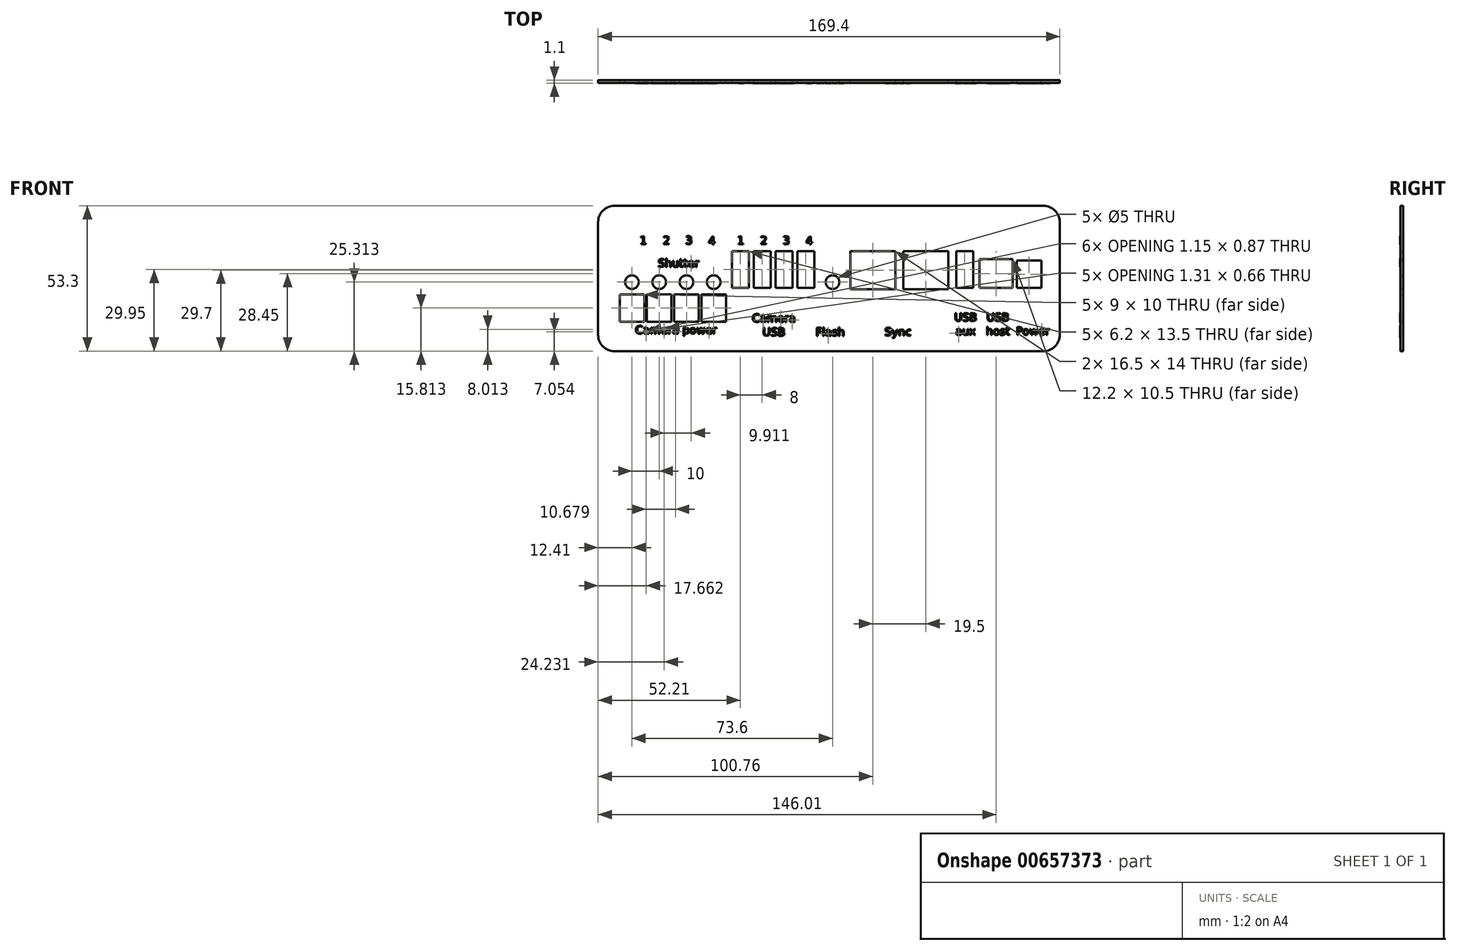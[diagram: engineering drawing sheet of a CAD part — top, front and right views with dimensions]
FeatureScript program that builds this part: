
annotation { "Feature Type Name" : "Feature", "Feature Type Description" : "" }
export const myFeature = defineFeature(function(context is Context, id is Id, definition is map)
    precondition{}
    {
        {
            var Q0;
            Q0=qCreatedBy(makeId("Front.planeOp"),FACE);
            var sketch = newSketch(context, id + "F0", { "sketchPlane" : qUnion([Q0])});
            skLineSegment(sketch, "E0", {"start": v(-108.51, -23.45) * mm, "end": v(48.89, -23.45) * mm});
            skLineSegment(sketch, "E1", {"start": v(48.89, 29.85) * mm, "end": v(-108.51, 29.85) * mm});
            skArc(sketch, "E2", {"start": v(-114.51, -17.45) * mm, "mid": v(-112.76, -21.7) * mm, "end": v(-108.51, -23.45) * mm});
            skLineSegment(sketch, "E3", {"start": v(54.89, -17.45) * mm, "end": v(54.89, 23.85) * mm});
            skArc(sketch, "E4", {"start": v(48.89, -23.45) * mm, "mid": v(53.13, -21.7) * mm, "end": v(54.89, -17.45) * mm});
            skArc(sketch, "E5", {"start": v(54.89, 23.85) * mm, "mid": v(53.13, 28.1) * mm, "end": v(48.89, 29.85) * mm});
            skLineSegment(sketch, "E6", {"start": v(-114.51, 23.85) * mm, "end": v(-114.51, -17.45) * mm});
            skArc(sketch, "E7", {"start": v(-108.51, 29.85) * mm, "mid": v(-112.76, 28.1) * mm, "end": v(-114.51, 23.85) * mm});
            skLineSegment(sketch, "E8.bottom", {"start": v(-59.2, -0.25) * mm, "end": v(-65.4, -0.25) * mm});
            skLineSegment(sketch, "E8.top", {"start": v(-59.2, 13.25) * mm, "end": v(-65.4, 13.25) * mm});
            skLineSegment(sketch, "E8.left", {"start": v(-59.2, -0.25) * mm, "end": v(-59.2, 13.25) * mm});
            skLineSegment(sketch, "E8.right", {"start": v(-65.4, -0.25) * mm, "end": v(-65.4, 13.25) * mm});
            skPoint(sketch, "E8.middle", {"position": v(-62.3, 6.5) * mm});
            skCircle(sketch, "E9", {"center": v(-72.1, 1.86) * mm, "radius": 2.5 * mm});
            skLineSegment(sketch, "E10.bottom", {"start": v(-67.6, -12.64) * mm, "end": v(-76.6, -12.64) * mm});
            skLineSegment(sketch, "E10.top", {"start": v(-67.6, -2.64) * mm, "end": v(-76.6, -2.64) * mm});
            skLineSegment(sketch, "E10.left", {"start": v(-67.6, -12.64) * mm, "end": v(-67.6, -2.64) * mm});
            skLineSegment(sketch, "E10.right", {"start": v(-76.6, -12.64) * mm, "end": v(-76.6, -2.64) * mm});
            skPoint(sketch, "E10.middle", {"position": v(-72.1, -7.64) * mm});
            skCircle(sketch, "E11.1.0.0", {"center": v(-82.1, 1.86) * mm, "radius": 2.5 * mm});
            skLineSegment(sketch, "E11.1.0.1", {"start": v(-77.6, -2.64) * mm, "end": v(-86.6, -2.64) * mm});
            skLineSegment(sketch, "E11.1.0.2", {"start": v(-77.6, -12.64) * mm, "end": v(-77.6, -2.64) * mm});
            skLineSegment(sketch, "E11.1.0.3", {"start": v(-77.6, -12.64) * mm, "end": v(-86.6, -12.64) * mm});
            skLineSegment(sketch, "E11.1.0.4", {"start": v(-86.6, -12.64) * mm, "end": v(-86.6, -2.64) * mm});
            skCircle(sketch, "E11.2.0.0", {"center": v(-92.1, 1.86) * mm, "radius": 2.5 * mm});
            skLineSegment(sketch, "E11.2.0.1", {"start": v(-87.6, -2.64) * mm, "end": v(-96.6, -2.64) * mm});
            skLineSegment(sketch, "E11.2.0.2", {"start": v(-87.6, -12.64) * mm, "end": v(-87.6, -2.64) * mm});
            skLineSegment(sketch, "E11.2.0.3", {"start": v(-87.6, -12.64) * mm, "end": v(-96.6, -12.64) * mm});
            skLineSegment(sketch, "E11.2.0.4", {"start": v(-96.6, -12.64) * mm, "end": v(-96.6, -2.64) * mm});
            skCircle(sketch, "E11.3.0.0", {"center": v(-102.1, 1.86) * mm, "radius": 2.5 * mm});
            skLineSegment(sketch, "E11.3.0.1", {"start": v(-97.6, -2.64) * mm, "end": v(-106.6, -2.64) * mm});
            skLineSegment(sketch, "E11.3.0.2", {"start": v(-97.6, -12.64) * mm, "end": v(-97.6, -2.64) * mm});
            skLineSegment(sketch, "E11.3.0.3", {"start": v(-97.6, -12.64) * mm, "end": v(-106.6, -12.64) * mm});
            skLineSegment(sketch, "E11.3.0.4", {"start": v(-106.6, -12.64) * mm, "end": v(-106.6, -2.64) * mm});
            skLineSegment(sketch, "E11.direction1", {"start": v(-72.1, 1.86) * mm, "end": v(-82.1, 1.86) * mm, "construction": true});
            skLineSegment(sketch, "E12.1.0.0", {"start": v(-51.2, -0.25) * mm, "end": v(-51.2, 13.25) * mm});
            skLineSegment(sketch, "E12.1.0.1", {"start": v(-51.2, 13.25) * mm, "end": v(-57.4, 13.25) * mm});
            skLineSegment(sketch, "E12.1.0.2", {"start": v(-57.4, -0.25) * mm, "end": v(-57.4, 13.25) * mm});
            skLineSegment(sketch, "E12.1.0.3", {"start": v(-51.2, -0.25) * mm, "end": v(-57.4, -0.25) * mm});
            skLineSegment(sketch, "E12.2.0.0", {"start": v(-43.2, -0.25) * mm, "end": v(-43.2, 13.25) * mm});
            skLineSegment(sketch, "E12.2.0.1", {"start": v(-43.2, 13.25) * mm, "end": v(-49.4, 13.25) * mm});
            skLineSegment(sketch, "E12.2.0.2", {"start": v(-49.4, -0.25) * mm, "end": v(-49.4, 13.25) * mm});
            skLineSegment(sketch, "E12.2.0.3", {"start": v(-43.2, -0.25) * mm, "end": v(-49.4, -0.25) * mm});
            skLineSegment(sketch, "E12.3.0.0", {"start": v(-35.2, -0.25) * mm, "end": v(-35.2, 13.25) * mm});
            skLineSegment(sketch, "E12.3.0.1", {"start": v(-35.2, 13.25) * mm, "end": v(-41.4, 13.25) * mm});
            skLineSegment(sketch, "E12.3.0.2", {"start": v(-41.4, -0.25) * mm, "end": v(-41.4, 13.25) * mm});
            skLineSegment(sketch, "E12.3.0.3", {"start": v(-35.2, -0.25) * mm, "end": v(-41.4, -0.25) * mm});
            skLineSegment(sketch, "E12.direction1", {"start": v(-59.2, -0.25) * mm, "end": v(-51.2, -0.25) * mm, "construction": true});
            skCircle(sketch, "E13", {"center": v(-28.5, 1.86) * mm, "radius": 2.5 * mm});
            skLineSegment(sketch, "E14.bottom", {"start": v(-5.5, 13.25) * mm, "end": v(-22, 13.25) * mm});
            skLineSegment(sketch, "E14.top", {"start": v(-5.5, -0.75) * mm, "end": v(-22, -0.75) * mm});
            skLineSegment(sketch, "E14.left", {"start": v(-5.5, 13.25) * mm, "end": v(-5.5, -0.75) * mm});
            skLineSegment(sketch, "E14.right", {"start": v(-22, 13.25) * mm, "end": v(-22, -0.75) * mm});
            skPoint(sketch, "E14.middle", {"position": v(-13.75, 6.25) * mm});
            skPoint(sketch, "E15.1.0.0", {"position": v(5.75, 6.25) * mm});
            skLineSegment(sketch, "E15.1.0.1", {"start": v(14, 13.25) * mm, "end": v(-2.5, 13.25) * mm});
            skLineSegment(sketch, "E15.1.0.2", {"start": v(14, 13.25) * mm, "end": v(14, -0.75) * mm});
            skLineSegment(sketch, "E15.1.0.3", {"start": v(14, -0.75) * mm, "end": v(-2.5, -0.75) * mm});
            skLineSegment(sketch, "E15.1.0.4", {"start": v(-2.5, 13.25) * mm, "end": v(-2.5, -0.75) * mm});
            skLineSegment(sketch, "E15.direction1", {"start": v(-13.75, 6.25) * mm, "end": v(5.75, 6.25) * mm, "construction": true});
            skLineSegment(sketch, "E16.bottom", {"start": v(23.1, -0.25) * mm, "end": v(16.9, -0.25) * mm});
            skLineSegment(sketch, "E16.top", {"start": v(23.1, 13.25) * mm, "end": v(16.9, 13.25) * mm});
            skLineSegment(sketch, "E16.left", {"start": v(23.1, -0.25) * mm, "end": v(23.1, 13.25) * mm});
            skLineSegment(sketch, "E16.right", {"start": v(16.9, -0.25) * mm, "end": v(16.9, 13.25) * mm});
            skPoint(sketch, "E16.middle", {"position": v(20, 6.5) * mm});
            skLineSegment(sketch, "E17.bottom", {"start": v(37.6, 10.25) * mm, "end": v(25.4, 10.25) * mm});
            skLineSegment(sketch, "E17.top", {"start": v(37.6, -0.25) * mm, "end": v(25.4, -0.25) * mm});
            skLineSegment(sketch, "E17.left", {"start": v(37.6, 10.25) * mm, "end": v(37.6, -0.25) * mm});
            skLineSegment(sketch, "E17.right", {"start": v(25.4, 10.25) * mm, "end": v(25.4, -0.25) * mm});
            skPoint(sketch, "E17.middle", {"position": v(31.5, 5) * mm});
            skLineSegment(sketch, "E18.bottom", {"start": v(48.1, -0.25) * mm, "end": v(39.1, -0.25) * mm});
            skLineSegment(sketch, "E18.top", {"start": v(48.1, 9.75) * mm, "end": v(39.1, 9.75) * mm});
            skLineSegment(sketch, "E18.left", {"start": v(48.1, -0.25) * mm, "end": v(48.1, 9.75) * mm});
            skLineSegment(sketch, "E18.right", {"start": v(39.1, -0.25) * mm, "end": v(39.1, 9.75) * mm});
            skPoint(sketch, "E18.middle", {"position": v(43.6, 4.75) * mm});
            skSolve(sketch);
        }
        {
            var Q0;
            Q0=makeQuery(id+"F0.imprint","IMPRINT",FACE,{"disambiguationData":[TD([[makeQuery(id+"F0.imprint","IMPRINT",EDGE,{"derivedFrom":sQuery(id+"F0.wireOp",EDGE,"E0")}),1.0]])]});
            extrude(context, id + "F1", {"entities" : qUnion([Q0]), "depth" : 1 * mm, "offsetDistance" : 25 * mm});
        }
        {
            var Q0;
            Q0=makeQuery(id+"F1.opExtrude","CAP_FACE",FACE,{"disambiguationData":[OSD([sQuery(id+"F0.wireOp",EDGE,"E0"),sQuery(id+"F0.wireOp",EDGE,"E1"),sQuery(id+"F0.wireOp",EDGE,"E2"),sQuery(id+"F0.wireOp",EDGE,"E3"),sQuery(id+"F0.wireOp",EDGE,"E4"),sQuery(id+"F0.wireOp",EDGE,"E5"),sQuery(id+"F0.wireOp",EDGE,"E6"),sQuery(id+"F0.wireOp",EDGE,"E7"),sQuery(id+"F0.wireOp",EDGE,"E8.bottom"),sQuery(id+"F0.wireOp",EDGE,"E8.top"),sQuery(id+"F0.wireOp",EDGE,"E8.left"),sQuery(id+"F0.wireOp",EDGE,"E8.right"),sQuery(id+"F0.wireOp",EDGE,"E9"),sQuery(id+"F0.wireOp",EDGE,"E10.bottom"),sQuery(id+"F0.wireOp",EDGE,"E10.top"),sQuery(id+"F0.wireOp",EDGE,"E10.left"),sQuery(id+"F0.wireOp",EDGE,"E10.right"),sQuery(id+"F0.wireOp",EDGE,"E11.1.0.0"),sQuery(id+"F0.wireOp",EDGE,"E11.1.0.1"),sQuery(id+"F0.wireOp",EDGE,"E11.1.0.2"),sQuery(id+"F0.wireOp",EDGE,"E11.1.0.3"),sQuery(id+"F0.wireOp",EDGE,"E11.1.0.4"),sQuery(id+"F0.wireOp",EDGE,"E11.2.0.0"),sQuery(id+"F0.wireOp",EDGE,"E11.2.0.1"),sQuery(id+"F0.wireOp",EDGE,"E11.2.0.2"),sQuery(id+"F0.wireOp",EDGE,"E11.2.0.3"),sQuery(id+"F0.wireOp",EDGE,"E11.2.0.4"),sQuery(id+"F0.wireOp",EDGE,"E11.3.0.0"),sQuery(id+"F0.wireOp",EDGE,"E11.3.0.1"),sQuery(id+"F0.wireOp",EDGE,"E11.3.0.2"),sQuery(id+"F0.wireOp",EDGE,"E11.3.0.3"),sQuery(id+"F0.wireOp",EDGE,"E11.3.0.4"),sQuery(id+"F0.wireOp",EDGE,"E12.1.0.0"),sQuery(id+"F0.wireOp",EDGE,"E12.1.0.1"),sQuery(id+"F0.wireOp",EDGE,"E12.1.0.2"),sQuery(id+"F0.wireOp",EDGE,"E12.1.0.3"),sQuery(id+"F0.wireOp",EDGE,"E12.2.0.0"),sQuery(id+"F0.wireOp",EDGE,"E12.2.0.1"),sQuery(id+"F0.wireOp",EDGE,"E12.2.0.2"),sQuery(id+"F0.wireOp",EDGE,"E12.2.0.3"),sQuery(id+"F0.wireOp",EDGE,"E12.3.0.0"),sQuery(id+"F0.wireOp",EDGE,"E12.3.0.1"),sQuery(id+"F0.wireOp",EDGE,"E12.3.0.2"),sQuery(id+"F0.wireOp",EDGE,"E12.3.0.3"),sQuery(id+"F0.wireOp",EDGE,"E13"),sQuery(id+"F0.wireOp",EDGE,"E14.bottom"),sQuery(id+"F0.wireOp",EDGE,"E14.top"),sQuery(id+"F0.wireOp",EDGE,"E14.left"),sQuery(id+"F0.wireOp",EDGE,"E14.right"),sQuery(id+"F0.wireOp",EDGE,"E15.1.0.1"),sQuery(id+"F0.wireOp",EDGE,"E15.1.0.2"),sQuery(id+"F0.wireOp",EDGE,"E15.1.0.3"),sQuery(id+"F0.wireOp",EDGE,"E15.1.0.4"),sQuery(id+"F0.wireOp",EDGE,"E16.bottom"),sQuery(id+"F0.wireOp",EDGE,"E16.top"),sQuery(id+"F0.wireOp",EDGE,"E16.left"),sQuery(id+"F0.wireOp",EDGE,"E16.right"),sQuery(id+"F0.wireOp",EDGE,"E17.bottom"),sQuery(id+"F0.wireOp",EDGE,"E17.top"),sQuery(id+"F0.wireOp",EDGE,"E17.left"),sQuery(id+"F0.wireOp",EDGE,"E17.right"),sQuery(id+"F0.wireOp",EDGE,"E18.bottom"),sQuery(id+"F0.wireOp",EDGE,"E18.top"),sQuery(id+"F0.wireOp",EDGE,"E18.left"),sQuery(id+"F0.wireOp",EDGE,"E18.right")])],"isStart":false});
            var sketch = newSketch(context, id + "F2", { "sketchPlane" : qUnion([Q0])});
            skLineSegment(sketch, "E19", {"start": v(-62.99, 16.07) * mm, "end": v(-62.33, 16.07) * mm});
            skLineSegment(sketch, "E20", {"start": v(-62.33, 16.07) * mm, "end": v(-62.33, 18.34) * mm});
            skLineSegment(sketch, "E21", {"start": v(-62.33, 18.34) * mm, "end": v(-63.05, 18.2) * mm});
            skLineSegment(sketch, "E22", {"start": v(-63.05, 18.2) * mm, "end": v(-63.05, 18.57) * mm});
            skLineSegment(sketch, "E23", {"start": v(-63.05, 18.57) * mm, "end": v(-62.33, 18.71) * mm});
            skLineSegment(sketch, "E24", {"start": v(-62.33, 18.71) * mm, "end": v(-61.93, 18.71) * mm});
            skLineSegment(sketch, "E25", {"start": v(-61.93, 18.71) * mm, "end": v(-61.93, 16.07) * mm});
            skLineSegment(sketch, "E26", {"start": v(-61.93, 16.07) * mm, "end": v(-61.27, 16.07) * mm});
            skLineSegment(sketch, "E27", {"start": v(-61.27, 16.07) * mm, "end": v(-61.27, 15.73) * mm});
            skLineSegment(sketch, "E28", {"start": v(-61.27, 15.73) * mm, "end": v(-62.99, 15.73) * mm});
            skLineSegment(sketch, "E29", {"start": v(-62.99, 15.73) * mm, "end": v(-62.99, 16.07) * mm});
            skLineSegment(sketch, "E30", {"start": v(-54.25, 16.05) * mm, "end": v(-52.85, 16.05) * mm});
            skLineSegment(sketch, "E31", {"start": v(-52.85, 16.05) * mm, "end": v(-52.85, 15.7) * mm});
            skLineSegment(sketch, "E32", {"start": v(-52.85, 15.7) * mm, "end": v(-54.74, 15.7) * mm});
            skLineSegment(sketch, "E33", {"start": v(-54.74, 15.7) * mm, "end": v(-54.74, 16.05) * mm});
            skLineSegment(sketch, "E34", {"start": v(-54.74, 16.05) * mm, "end": v(-54.11, 16.68) * mm});
            skLineSegment(sketch, "E35", {"start": v(-54.11, 16.68) * mm, "end": v(-53.61, 17.2) * mm});
            skLineSegment(sketch, "E36", {"start": v(-53.61, 17.2) * mm, "end": v(-53.34, 17.56) * mm});
            skLineSegment(sketch, "E37", {"start": v(-53.34, 17.56) * mm, "end": v(-53.27, 17.86) * mm});
            skLineSegment(sketch, "E38", {"start": v(-53.27, 17.86) * mm, "end": v(-53.43, 18.25) * mm});
            skLineSegment(sketch, "E39", {"start": v(-53.43, 18.25) * mm, "end": v(-53.87, 18.4) * mm});
            skLineSegment(sketch, "E40", {"start": v(-53.87, 18.4) * mm, "end": v(-54.27, 18.33) * mm});
            skLineSegment(sketch, "E41", {"start": v(-54.27, 18.33) * mm, "end": v(-54.72, 18.13) * mm});
            skLineSegment(sketch, "E42", {"start": v(-54.72, 18.13) * mm, "end": v(-54.72, 18.54) * mm});
            skLineSegment(sketch, "E43", {"start": v(-54.72, 18.54) * mm, "end": v(-54.26, 18.69) * mm});
            skLineSegment(sketch, "E44", {"start": v(-54.26, 18.69) * mm, "end": v(-53.87, 18.74) * mm});
            skLineSegment(sketch, "E45", {"start": v(-53.87, 18.74) * mm, "end": v(-53.14, 18.5) * mm});
            skLineSegment(sketch, "E46", {"start": v(-53.14, 18.5) * mm, "end": v(-52.86, 17.89) * mm});
            skLineSegment(sketch, "E47", {"start": v(-52.86, 17.89) * mm, "end": v(-52.93, 17.54) * mm});
            skLineSegment(sketch, "E48", {"start": v(-52.93, 17.54) * mm, "end": v(-53.18, 17.15) * mm});
            skLineSegment(sketch, "E49", {"start": v(-53.18, 17.15) * mm, "end": v(-53.5, 16.82) * mm});
            skLineSegment(sketch, "E50", {"start": v(-53.5, 16.82) * mm, "end": v(-54.25, 16.05) * mm});
            skLineSegment(sketch, "E51", {"start": v(-45.05, 17.34) * mm, "end": v(-44.6, 17.08) * mm});
            skLineSegment(sketch, "E52", {"start": v(-44.6, 17.08) * mm, "end": v(-44.44, 16.6) * mm});
            skLineSegment(sketch, "E53", {"start": v(-44.44, 16.6) * mm, "end": v(-44.74, 15.92) * mm});
            skLineSegment(sketch, "E54", {"start": v(-44.74, 15.92) * mm, "end": v(-45.6, 15.68) * mm});
            skLineSegment(sketch, "E55", {"start": v(-45.6, 15.68) * mm, "end": v(-46, 15.72) * mm});
            skLineSegment(sketch, "E56", {"start": v(-46, 15.72) * mm, "end": v(-46.4, 15.83) * mm});
            skLineSegment(sketch, "E57", {"start": v(-46.4, 15.83) * mm, "end": v(-46.4, 16.21) * mm});
            skLineSegment(sketch, "E58", {"start": v(-46.4, 16.21) * mm, "end": v(-46.03, 16.07) * mm});
            skLineSegment(sketch, "E59", {"start": v(-46.03, 16.07) * mm, "end": v(-45.62, 16.02) * mm});
            skLineSegment(sketch, "E60", {"start": v(-45.62, 16.02) * mm, "end": v(-45.04, 16.17) * mm});
            skLineSegment(sketch, "E61", {"start": v(-45.04, 16.17) * mm, "end": v(-44.84, 16.6) * mm});
            skLineSegment(sketch, "E62", {"start": v(-44.84, 16.6) * mm, "end": v(-45.03, 17.01) * mm});
            skLineSegment(sketch, "E63", {"start": v(-45.03, 17.01) * mm, "end": v(-45.54, 17.16) * mm});
            skLineSegment(sketch, "E64", {"start": v(-45.54, 17.16) * mm, "end": v(-45.89, 17.16) * mm});
            skLineSegment(sketch, "E65", {"start": v(-45.89, 17.16) * mm, "end": v(-45.89, 17.5) * mm});
            skLineSegment(sketch, "E66", {"start": v(-45.89, 17.5) * mm, "end": v(-45.52, 17.5) * mm});
            skLineSegment(sketch, "E67", {"start": v(-45.52, 17.5) * mm, "end": v(-45.07, 17.61) * mm});
            skLineSegment(sketch, "E68", {"start": v(-45.07, 17.61) * mm, "end": v(-44.91, 17.95) * mm});
            skLineSegment(sketch, "E69", {"start": v(-44.91, 17.95) * mm, "end": v(-45.07, 18.3) * mm});
            skLineSegment(sketch, "E70", {"start": v(-45.07, 18.3) * mm, "end": v(-45.54, 18.43) * mm});
            skLineSegment(sketch, "E71", {"start": v(-45.54, 18.43) * mm, "end": v(-45.9, 18.4) * mm});
            skLineSegment(sketch, "E72", {"start": v(-45.9, 18.4) * mm, "end": v(-46.31, 18.28) * mm});
            skLineSegment(sketch, "E73", {"start": v(-46.31, 18.28) * mm, "end": v(-46.31, 18.64) * mm});
            skLineSegment(sketch, "E74", {"start": v(-46.31, 18.64) * mm, "end": v(-45.88, 18.73) * mm});
            skLineSegment(sketch, "E75", {"start": v(-45.88, 18.73) * mm, "end": v(-45.5, 18.77) * mm});
            skLineSegment(sketch, "E76", {"start": v(-45.5, 18.77) * mm, "end": v(-44.78, 18.56) * mm});
            skLineSegment(sketch, "E77", {"start": v(-44.78, 18.56) * mm, "end": v(-44.51, 18) * mm});
            skLineSegment(sketch, "E78", {"start": v(-44.51, 18) * mm, "end": v(-44.65, 17.58) * mm});
            skLineSegment(sketch, "E79", {"start": v(-44.65, 17.58) * mm, "end": v(-45.05, 17.34) * mm});
            skLineSegment(sketch, "E80", {"start": v(-36.8, 18.22) * mm, "end": v(-37.8, 16.63) * mm});
            skLineSegment(sketch, "E81", {"start": v(-37.8, 16.63) * mm, "end": v(-36.8, 16.63) * mm});
            skLineSegment(sketch, "E82", {"start": v(-36.8, 16.63) * mm, "end": v(-36.8, 18.22) * mm});
            skLineSegment(sketch, "E83", {"start": v(-36.9, 18.57) * mm, "end": v(-36.4, 18.57) * mm});
            skLineSegment(sketch, "E84", {"start": v(-36.4, 18.57) * mm, "end": v(-36.4, 16.63) * mm});
            skLineSegment(sketch, "E85", {"start": v(-36.4, 16.63) * mm, "end": v(-35.97, 16.63) * mm});
            skLineSegment(sketch, "E86", {"start": v(-35.97, 16.63) * mm, "end": v(-35.97, 16.3) * mm});
            skLineSegment(sketch, "E87", {"start": v(-35.97, 16.3) * mm, "end": v(-36.4, 16.3) * mm});
            skLineSegment(sketch, "E88", {"start": v(-36.4, 16.3) * mm, "end": v(-36.4, 15.6) * mm});
            skLineSegment(sketch, "E89", {"start": v(-36.4, 15.6) * mm, "end": v(-36.8, 15.6) * mm});
            skLineSegment(sketch, "E90", {"start": v(-36.8, 15.6) * mm, "end": v(-36.8, 16.3) * mm});
            skLineSegment(sketch, "E91", {"start": v(-36.8, 16.3) * mm, "end": v(-38.14, 16.3) * mm});
            skLineSegment(sketch, "E92", {"start": v(-38.14, 16.3) * mm, "end": v(-38.14, 16.69) * mm});
            skLineSegment(sketch, "E93", {"start": v(-38.14, 16.69) * mm, "end": v(-36.9, 18.57) * mm});
            skLineSegment(sketch, "E94", {"start": v(-98.26, -14.33) * mm, "end": v(-98.26, -14.76) * mm});
            skLineSegment(sketch, "E95", {"start": v(-98.26, -14.76) * mm, "end": v(-98.7, -14.48) * mm});
            skLineSegment(sketch, "E96", {"start": v(-98.7, -14.48) * mm, "end": v(-99.19, -14.38) * mm});
            skLineSegment(sketch, "E97", {"start": v(-99.19, -14.38) * mm, "end": v(-99.97, -14.7) * mm});
            skLineSegment(sketch, "E98", {"start": v(-99.97, -14.7) * mm, "end": v(-100.24, -15.6) * mm});
            skLineSegment(sketch, "E99", {"start": v(-100.24, -15.6) * mm, "end": v(-99.97, -16.5) * mm});
            skLineSegment(sketch, "E100", {"start": v(-99.97, -16.5) * mm, "end": v(-99.19, -16.8) * mm});
            skLineSegment(sketch, "E101", {"start": v(-99.19, -16.8) * mm, "end": v(-98.7, -16.72) * mm});
            skLineSegment(sketch, "E102", {"start": v(-98.7, -16.72) * mm, "end": v(-98.26, -16.43) * mm});
            skLineSegment(sketch, "E103", {"start": v(-98.26, -16.43) * mm, "end": v(-98.26, -16.85) * mm});
            skLineSegment(sketch, "E104", {"start": v(-98.26, -16.85) * mm, "end": v(-98.71, -17.07) * mm});
            skLineSegment(sketch, "E105", {"start": v(-98.71, -17.07) * mm, "end": v(-99.2, -17.14) * mm});
            skLineSegment(sketch, "E106", {"start": v(-99.2, -17.14) * mm, "end": v(-99.81, -17.04) * mm});
            skLineSegment(sketch, "E107", {"start": v(-99.81, -17.04) * mm, "end": v(-100.27, -16.73) * mm});
            skLineSegment(sketch, "E108", {"start": v(-100.27, -16.73) * mm, "end": v(-100.57, -16.24) * mm});
            skLineSegment(sketch, "E109", {"start": v(-100.57, -16.24) * mm, "end": v(-100.66, -15.6) * mm});
            skLineSegment(sketch, "E110", {"start": v(-100.66, -15.6) * mm, "end": v(-100.57, -14.95) * mm});
            skLineSegment(sketch, "E111", {"start": v(-100.57, -14.95) * mm, "end": v(-100.27, -14.47) * mm});
            skLineSegment(sketch, "E112", {"start": v(-100.27, -14.47) * mm, "end": v(-99.81, -14.16) * mm});
            skLineSegment(sketch, "E113", {"start": v(-99.81, -14.16) * mm, "end": v(-99.2, -14.05) * mm});
            skLineSegment(sketch, "E114", {"start": v(-99.2, -14.05) * mm, "end": v(-98.7, -14.12) * mm});
            skLineSegment(sketch, "E115", {"start": v(-98.7, -14.12) * mm, "end": v(-98.26, -14.33) * mm});
            skLineSegment(sketch, "E116", {"start": v(-96.64, -15.96) * mm, "end": v(-97.25, -16.06) * mm});
            skLineSegment(sketch, "E117", {"start": v(-97.25, -16.06) * mm, "end": v(-97.42, -16.4) * mm});
            skLineSegment(sketch, "E118", {"start": v(-97.42, -16.4) * mm, "end": v(-97.3, -16.72) * mm});
            skLineSegment(sketch, "E119", {"start": v(-97.3, -16.72) * mm, "end": v(-96.95, -16.83) * mm});
            skLineSegment(sketch, "E120", {"start": v(-96.95, -16.83) * mm, "end": v(-96.46, -16.62) * mm});
            skLineSegment(sketch, "E121", {"start": v(-96.46, -16.62) * mm, "end": v(-96.27, -16.04) * mm});
            skLineSegment(sketch, "E122", {"start": v(-96.27, -16.04) * mm, "end": v(-96.27, -15.96) * mm});
            skLineSegment(sketch, "E123", {"start": v(-96.27, -15.96) * mm, "end": v(-96.64, -15.96) * mm});
            skLineSegment(sketch, "E124", {"start": v(-95.9, -15.8) * mm, "end": v(-95.9, -17.08) * mm});
            skLineSegment(sketch, "E125", {"start": v(-95.9, -17.08) * mm, "end": v(-96.27, -17.08) * mm});
            skLineSegment(sketch, "E126", {"start": v(-96.27, -17.08) * mm, "end": v(-96.27, -16.74) * mm});
            skLineSegment(sketch, "E127", {"start": v(-96.27, -16.74) * mm, "end": v(-96.58, -17.04) * mm});
            skLineSegment(sketch, "E128", {"start": v(-96.58, -17.04) * mm, "end": v(-97.04, -17.14) * mm});
            skLineSegment(sketch, "E129", {"start": v(-97.04, -17.14) * mm, "end": v(-97.59, -16.95) * mm});
            skLineSegment(sketch, "E130", {"start": v(-97.59, -16.95) * mm, "end": v(-97.8, -16.43) * mm});
            skLineSegment(sketch, "E131", {"start": v(-97.8, -16.43) * mm, "end": v(-97.54, -15.86) * mm});
            skLineSegment(sketch, "E132", {"start": v(-97.54, -15.86) * mm, "end": v(-96.79, -15.67) * mm});
            skLineSegment(sketch, "E133", {"start": v(-96.79, -15.67) * mm, "end": v(-96.27, -15.67) * mm});
            skLineSegment(sketch, "E134", {"start": v(-96.27, -15.67) * mm, "end": v(-96.27, -15.64) * mm});
            skLineSegment(sketch, "E135", {"start": v(-96.27, -15.64) * mm, "end": v(-96.44, -15.25) * mm});
            skLineSegment(sketch, "E136", {"start": v(-96.44, -15.25) * mm, "end": v(-96.9, -15.1) * mm});
            skLineSegment(sketch, "E137", {"start": v(-96.9, -15.1) * mm, "end": v(-97.28, -15.15) * mm});
            skLineSegment(sketch, "E138", {"start": v(-97.28, -15.15) * mm, "end": v(-97.63, -15.29) * mm});
            skLineSegment(sketch, "E139", {"start": v(-97.63, -15.29) * mm, "end": v(-97.63, -14.95) * mm});
            skLineSegment(sketch, "E140", {"start": v(-97.63, -14.95) * mm, "end": v(-97.24, -14.83) * mm});
            skLineSegment(sketch, "E141", {"start": v(-97.24, -14.83) * mm, "end": v(-96.87, -14.8) * mm});
            skLineSegment(sketch, "E142", {"start": v(-96.87, -14.8) * mm, "end": v(-96.14, -15.05) * mm});
            skLineSegment(sketch, "E143", {"start": v(-96.14, -15.05) * mm, "end": v(-95.9, -15.8) * mm});
            skLineSegment(sketch, "E144", {"start": v(-93.4, -15.28) * mm, "end": v(-93.08, -14.91) * mm});
            skLineSegment(sketch, "E145", {"start": v(-93.08, -14.91) * mm, "end": v(-92.63, -14.8) * mm});
            skLineSegment(sketch, "E146", {"start": v(-92.63, -14.8) * mm, "end": v(-92.1, -15.04) * mm});
            skLineSegment(sketch, "E147", {"start": v(-92.1, -15.04) * mm, "end": v(-91.9, -15.73) * mm});
            skLineSegment(sketch, "E148", {"start": v(-91.9, -15.73) * mm, "end": v(-91.9, -17.08) * mm});
            skLineSegment(sketch, "E149", {"start": v(-91.9, -17.08) * mm, "end": v(-92.27, -17.08) * mm});
            skLineSegment(sketch, "E150", {"start": v(-92.27, -17.08) * mm, "end": v(-92.27, -15.75) * mm});
            skLineSegment(sketch, "E151", {"start": v(-92.27, -15.75) * mm, "end": v(-92.38, -15.27) * mm});
            skLineSegment(sketch, "E152", {"start": v(-92.38, -15.27) * mm, "end": v(-92.73, -15.11) * mm});
            skLineSegment(sketch, "E153", {"start": v(-92.73, -15.11) * mm, "end": v(-93.18, -15.3) * mm});
            skLineSegment(sketch, "E154", {"start": v(-93.18, -15.3) * mm, "end": v(-93.35, -15.82) * mm});
            skLineSegment(sketch, "E155", {"start": v(-93.35, -15.82) * mm, "end": v(-93.35, -17.08) * mm});
            skLineSegment(sketch, "E156", {"start": v(-93.35, -17.08) * mm, "end": v(-93.72, -17.08) * mm});
            skLineSegment(sketch, "E157", {"start": v(-93.72, -17.08) * mm, "end": v(-93.72, -15.75) * mm});
            skLineSegment(sketch, "E158", {"start": v(-93.72, -15.75) * mm, "end": v(-93.83, -15.27) * mm});
            skLineSegment(sketch, "E159", {"start": v(-93.83, -15.27) * mm, "end": v(-94.18, -15.11) * mm});
            skLineSegment(sketch, "E160", {"start": v(-94.18, -15.11) * mm, "end": v(-94.63, -15.3) * mm});
            skLineSegment(sketch, "E161", {"start": v(-94.63, -15.3) * mm, "end": v(-94.8, -15.82) * mm});
            skLineSegment(sketch, "E162", {"start": v(-94.8, -15.82) * mm, "end": v(-94.8, -17.08) * mm});
            skLineSegment(sketch, "E163", {"start": v(-94.8, -17.08) * mm, "end": v(-95.16, -17.08) * mm});
            skLineSegment(sketch, "E164", {"start": v(-95.16, -17.08) * mm, "end": v(-95.16, -14.85) * mm});
            skLineSegment(sketch, "E165", {"start": v(-95.16, -14.85) * mm, "end": v(-94.8, -14.85) * mm});
            skLineSegment(sketch, "E166", {"start": v(-94.8, -14.85) * mm, "end": v(-94.8, -15.2) * mm});
            skLineSegment(sketch, "E167", {"start": v(-94.8, -15.2) * mm, "end": v(-94.5, -14.9) * mm});
            skLineSegment(sketch, "E168", {"start": v(-94.5, -14.9) * mm, "end": v(-94.08, -14.8) * mm});
            skLineSegment(sketch, "E169", {"start": v(-94.08, -14.8) * mm, "end": v(-93.66, -14.92) * mm});
            skLineSegment(sketch, "E170", {"start": v(-93.66, -14.92) * mm, "end": v(-93.4, -15.28) * mm});
            skLineSegment(sketch, "E171", {"start": v(-89.26, -15.87) * mm, "end": v(-89.26, -16.05) * mm});
            skLineSegment(sketch, "E172", {"start": v(-89.26, -16.05) * mm, "end": v(-90.94, -16.05) * mm});
            skLineSegment(sketch, "E173", {"start": v(-90.94, -16.05) * mm, "end": v(-90.72, -16.63) * mm});
            skLineSegment(sketch, "E174", {"start": v(-90.72, -16.63) * mm, "end": v(-90.15, -16.83) * mm});
            skLineSegment(sketch, "E175", {"start": v(-90.15, -16.83) * mm, "end": v(-89.74, -16.78) * mm});
            skLineSegment(sketch, "E176", {"start": v(-89.74, -16.78) * mm, "end": v(-89.34, -16.62) * mm});
            skLineSegment(sketch, "E177", {"start": v(-89.34, -16.62) * mm, "end": v(-89.34, -16.97) * mm});
            skLineSegment(sketch, "E178", {"start": v(-89.34, -16.97) * mm, "end": v(-89.75, -17.1) * mm});
            skLineSegment(sketch, "E179", {"start": v(-89.75, -17.1) * mm, "end": v(-90.17, -17.14) * mm});
            skLineSegment(sketch, "E180", {"start": v(-90.17, -17.14) * mm, "end": v(-91.02, -16.83) * mm});
            skLineSegment(sketch, "E181", {"start": v(-91.02, -16.83) * mm, "end": v(-91.33, -15.99) * mm});
            skLineSegment(sketch, "E182", {"start": v(-91.33, -15.99) * mm, "end": v(-91.03, -15.12) * mm});
            skLineSegment(sketch, "E183", {"start": v(-91.03, -15.12) * mm, "end": v(-90.23, -14.8) * mm});
            skLineSegment(sketch, "E184", {"start": v(-90.23, -14.8) * mm, "end": v(-89.52, -15.09) * mm});
            skLineSegment(sketch, "E185", {"start": v(-89.52, -15.09) * mm, "end": v(-89.26, -15.87) * mm});
            skLineSegment(sketch, "E186", {"start": v(-89.62, -15.77) * mm, "end": v(-89.8, -15.28) * mm});
            skLineSegment(sketch, "E187", {"start": v(-89.8, -15.28) * mm, "end": v(-90.23, -15.1) * mm});
            skLineSegment(sketch, "E188", {"start": v(-90.23, -15.1) * mm, "end": v(-90.72, -15.28) * mm});
            skLineSegment(sketch, "E189", {"start": v(-90.72, -15.28) * mm, "end": v(-90.93, -15.77) * mm});
            skLineSegment(sketch, "E190", {"start": v(-90.93, -15.77) * mm, "end": v(-89.62, -15.77) * mm});
            skLineSegment(sketch, "E191", {"start": v(-87.36, -15.2) * mm, "end": v(-87.5, -15.14) * mm});
            skLineSegment(sketch, "E192", {"start": v(-87.5, -15.14) * mm, "end": v(-87.66, -15.12) * mm});
            skLineSegment(sketch, "E193", {"start": v(-87.66, -15.12) * mm, "end": v(-88.14, -15.32) * mm});
            skLineSegment(sketch, "E194", {"start": v(-88.14, -15.32) * mm, "end": v(-88.3, -15.9) * mm});
            skLineSegment(sketch, "E195", {"start": v(-88.3, -15.9) * mm, "end": v(-88.3, -17.08) * mm});
            skLineSegment(sketch, "E196", {"start": v(-88.3, -17.08) * mm, "end": v(-88.67, -17.08) * mm});
            skLineSegment(sketch, "E197", {"start": v(-88.67, -17.08) * mm, "end": v(-88.67, -14.85) * mm});
            skLineSegment(sketch, "E198", {"start": v(-88.67, -14.85) * mm, "end": v(-88.3, -14.85) * mm});
            skLineSegment(sketch, "E199", {"start": v(-88.3, -14.85) * mm, "end": v(-88.3, -15.2) * mm});
            skLineSegment(sketch, "E200", {"start": v(-88.3, -15.2) * mm, "end": v(-88, -14.9) * mm});
            skLineSegment(sketch, "E201", {"start": v(-88, -14.9) * mm, "end": v(-87.55, -14.8) * mm});
            skLineSegment(sketch, "E202", {"start": v(-87.55, -14.8) * mm, "end": v(-87.47, -14.8) * mm});
            skLineSegment(sketch, "E203", {"start": v(-87.47, -14.8) * mm, "end": v(-87.36, -14.81) * mm});
            skLineSegment(sketch, "E204", {"start": v(-87.36, -14.81) * mm, "end": v(-87.36, -15.2) * mm});
            skLineSegment(sketch, "E205", {"start": v(-85.96, -15.96) * mm, "end": v(-86.57, -16.06) * mm});
            skLineSegment(sketch, "E206", {"start": v(-86.57, -16.06) * mm, "end": v(-86.75, -16.4) * mm});
            skLineSegment(sketch, "E207", {"start": v(-86.75, -16.4) * mm, "end": v(-86.62, -16.72) * mm});
            skLineSegment(sketch, "E208", {"start": v(-86.62, -16.72) * mm, "end": v(-86.27, -16.83) * mm});
            skLineSegment(sketch, "E209", {"start": v(-86.27, -16.83) * mm, "end": v(-85.78, -16.62) * mm});
            skLineSegment(sketch, "E210", {"start": v(-85.78, -16.62) * mm, "end": v(-85.6, -16.04) * mm});
            skLineSegment(sketch, "E211", {"start": v(-85.6, -16.04) * mm, "end": v(-85.6, -15.96) * mm});
            skLineSegment(sketch, "E212", {"start": v(-85.6, -15.96) * mm, "end": v(-85.96, -15.96) * mm});
            skLineSegment(sketch, "E213", {"start": v(-85.23, -15.8) * mm, "end": v(-85.23, -17.08) * mm});
            skLineSegment(sketch, "E214", {"start": v(-85.23, -17.08) * mm, "end": v(-85.6, -17.08) * mm});
            skLineSegment(sketch, "E215", {"start": v(-85.6, -17.08) * mm, "end": v(-85.6, -16.74) * mm});
            skLineSegment(sketch, "E216", {"start": v(-85.6, -16.74) * mm, "end": v(-85.9, -17.04) * mm});
            skLineSegment(sketch, "E217", {"start": v(-85.9, -17.04) * mm, "end": v(-86.37, -17.14) * mm});
            skLineSegment(sketch, "E218", {"start": v(-86.37, -17.14) * mm, "end": v(-86.91, -16.95) * mm});
            skLineSegment(sketch, "E219", {"start": v(-86.91, -16.95) * mm, "end": v(-87.11, -16.43) * mm});
            skLineSegment(sketch, "E220", {"start": v(-87.11, -16.43) * mm, "end": v(-86.86, -15.86) * mm});
            skLineSegment(sketch, "E221", {"start": v(-86.86, -15.86) * mm, "end": v(-86.1, -15.67) * mm});
            skLineSegment(sketch, "E222", {"start": v(-86.1, -15.67) * mm, "end": v(-85.6, -15.67) * mm});
            skLineSegment(sketch, "E223", {"start": v(-85.6, -15.67) * mm, "end": v(-85.6, -15.64) * mm});
            skLineSegment(sketch, "E224", {"start": v(-85.6, -15.64) * mm, "end": v(-85.76, -15.25) * mm});
            skLineSegment(sketch, "E225", {"start": v(-85.76, -15.25) * mm, "end": v(-86.23, -15.1) * mm});
            skLineSegment(sketch, "E226", {"start": v(-86.23, -15.1) * mm, "end": v(-86.6, -15.15) * mm});
            skLineSegment(sketch, "E227", {"start": v(-86.6, -15.15) * mm, "end": v(-86.95, -15.29) * mm});
            skLineSegment(sketch, "E228", {"start": v(-86.95, -15.29) * mm, "end": v(-86.95, -14.95) * mm});
            skLineSegment(sketch, "E229", {"start": v(-86.95, -14.95) * mm, "end": v(-86.56, -14.83) * mm});
            skLineSegment(sketch, "E230", {"start": v(-86.56, -14.83) * mm, "end": v(-86.2, -14.8) * mm});
            skLineSegment(sketch, "E231", {"start": v(-86.2, -14.8) * mm, "end": v(-85.47, -15.05) * mm});
            skLineSegment(sketch, "E232", {"start": v(-85.47, -15.05) * mm, "end": v(-85.23, -15.8) * mm});
            skLineSegment(sketch, "E233", {"start": v(-82.81, -16.75) * mm, "end": v(-82.81, -17.93) * mm});
            skLineSegment(sketch, "E234", {"start": v(-82.81, -17.93) * mm, "end": v(-83.18, -17.93) * mm});
            skLineSegment(sketch, "E235", {"start": v(-83.18, -17.93) * mm, "end": v(-83.18, -14.85) * mm});
            skLineSegment(sketch, "E236", {"start": v(-83.18, -14.85) * mm, "end": v(-82.81, -14.85) * mm});
            skLineSegment(sketch, "E237", {"start": v(-82.81, -14.85) * mm, "end": v(-82.81, -15.19) * mm});
            skLineSegment(sketch, "E238", {"start": v(-82.81, -15.19) * mm, "end": v(-82.52, -14.9) * mm});
            skLineSegment(sketch, "E239", {"start": v(-82.52, -14.9) * mm, "end": v(-82.1, -14.8) * mm});
            skLineSegment(sketch, "E240", {"start": v(-82.1, -14.8) * mm, "end": v(-81.44, -15.12) * mm});
            skLineSegment(sketch, "E241", {"start": v(-81.44, -15.12) * mm, "end": v(-81.19, -15.97) * mm});
            skLineSegment(sketch, "E242", {"start": v(-81.19, -15.97) * mm, "end": v(-81.44, -16.82) * mm});
            skLineSegment(sketch, "E243", {"start": v(-81.44, -16.82) * mm, "end": v(-82.1, -17.14) * mm});
            skLineSegment(sketch, "E244", {"start": v(-82.1, -17.14) * mm, "end": v(-82.52, -17.04) * mm});
            skLineSegment(sketch, "E245", {"start": v(-82.52, -17.04) * mm, "end": v(-82.81, -16.75) * mm});
            skLineSegment(sketch, "E246", {"start": v(-81.57, -15.97) * mm, "end": v(-81.73, -15.33) * mm});
            skLineSegment(sketch, "E247", {"start": v(-81.73, -15.33) * mm, "end": v(-82.2, -15.1) * mm});
            skLineSegment(sketch, "E248", {"start": v(-82.2, -15.1) * mm, "end": v(-82.65, -15.33) * mm});
            skLineSegment(sketch, "E249", {"start": v(-82.65, -15.33) * mm, "end": v(-82.81, -15.97) * mm});
            skLineSegment(sketch, "E250", {"start": v(-82.81, -15.97) * mm, "end": v(-82.65, -16.6) * mm});
            skLineSegment(sketch, "E251", {"start": v(-82.65, -16.6) * mm, "end": v(-82.2, -16.83) * mm});
            skLineSegment(sketch, "E252", {"start": v(-82.2, -16.83) * mm, "end": v(-81.73, -16.6) * mm});
            skLineSegment(sketch, "E253", {"start": v(-81.73, -16.6) * mm, "end": v(-81.57, -15.97) * mm});
            skLineSegment(sketch, "E254", {"start": v(-79.71, -15.1) * mm, "end": v(-80.18, -15.34) * mm});
            skLineSegment(sketch, "E255", {"start": v(-80.18, -15.34) * mm, "end": v(-80.35, -15.97) * mm});
            skLineSegment(sketch, "E256", {"start": v(-80.35, -15.97) * mm, "end": v(-80.18, -16.6) * mm});
            skLineSegment(sketch, "E257", {"start": v(-80.18, -16.6) * mm, "end": v(-79.71, -16.83) * mm});
            skLineSegment(sketch, "E258", {"start": v(-79.71, -16.83) * mm, "end": v(-79.25, -16.6) * mm});
            skLineSegment(sketch, "E259", {"start": v(-79.25, -16.6) * mm, "end": v(-79.08, -15.97) * mm});
            skLineSegment(sketch, "E260", {"start": v(-79.08, -15.97) * mm, "end": v(-79.25, -15.34) * mm});
            skLineSegment(sketch, "E261", {"start": v(-79.25, -15.34) * mm, "end": v(-79.71, -15.1) * mm});
            skLineSegment(sketch, "E262", {"start": v(-79.71, -14.8) * mm, "end": v(-78.96, -15.1) * mm});
            skLineSegment(sketch, "E263", {"start": v(-78.96, -15.1) * mm, "end": v(-78.69, -15.97) * mm});
            skLineSegment(sketch, "E264", {"start": v(-78.69, -15.97) * mm, "end": v(-78.96, -16.83) * mm});
            skLineSegment(sketch, "E265", {"start": v(-78.96, -16.83) * mm, "end": v(-79.71, -17.14) * mm});
            skLineSegment(sketch, "E266", {"start": v(-79.71, -17.14) * mm, "end": v(-80.47, -16.83) * mm});
            skLineSegment(sketch, "E267", {"start": v(-80.47, -16.83) * mm, "end": v(-80.74, -15.97) * mm});
            skLineSegment(sketch, "E268", {"start": v(-80.74, -15.97) * mm, "end": v(-80.47, -15.1) * mm});
            skLineSegment(sketch, "E269", {"start": v(-80.47, -15.1) * mm, "end": v(-79.71, -14.8) * mm});
            skLineSegment(sketch, "E270", {"start": v(-78.3, -14.85) * mm, "end": v(-77.93, -14.85) * mm});
            skLineSegment(sketch, "E271", {"start": v(-77.93, -14.85) * mm, "end": v(-77.47, -16.6) * mm});
            skLineSegment(sketch, "E272", {"start": v(-77.47, -16.6) * mm, "end": v(-77.01, -14.85) * mm});
            skLineSegment(sketch, "E273", {"start": v(-77.01, -14.85) * mm, "end": v(-76.58, -14.85) * mm});
            skLineSegment(sketch, "E274", {"start": v(-76.58, -14.85) * mm, "end": v(-76.12, -16.6) * mm});
            skLineSegment(sketch, "E275", {"start": v(-76.12, -16.6) * mm, "end": v(-75.66, -14.85) * mm});
            skLineSegment(sketch, "E276", {"start": v(-75.66, -14.85) * mm, "end": v(-75.3, -14.85) * mm});
            skLineSegment(sketch, "E277", {"start": v(-75.3, -14.85) * mm, "end": v(-75.88, -17.08) * mm});
            skLineSegment(sketch, "E278", {"start": v(-75.88, -17.08) * mm, "end": v(-76.31, -17.08) * mm});
            skLineSegment(sketch, "E279", {"start": v(-76.31, -17.08) * mm, "end": v(-76.8, -15.25) * mm});
            skLineSegment(sketch, "E280", {"start": v(-76.8, -15.25) * mm, "end": v(-77.28, -17.08) * mm});
            skLineSegment(sketch, "E281", {"start": v(-77.28, -17.08) * mm, "end": v(-77.7, -17.08) * mm});
            skLineSegment(sketch, "E282", {"start": v(-77.7, -17.08) * mm, "end": v(-78.3, -14.85) * mm});
            skLineSegment(sketch, "E283", {"start": v(-72.83, -15.87) * mm, "end": v(-72.83, -16.05) * mm});
            skLineSegment(sketch, "E284", {"start": v(-72.83, -16.05) * mm, "end": v(-74.52, -16.05) * mm});
            skLineSegment(sketch, "E285", {"start": v(-74.52, -16.05) * mm, "end": v(-74.29, -16.63) * mm});
            skLineSegment(sketch, "E286", {"start": v(-74.29, -16.63) * mm, "end": v(-73.72, -16.83) * mm});
            skLineSegment(sketch, "E287", {"start": v(-73.72, -16.83) * mm, "end": v(-73.3, -16.78) * mm});
            skLineSegment(sketch, "E288", {"start": v(-73.3, -16.78) * mm, "end": v(-72.92, -16.62) * mm});
            skLineSegment(sketch, "E289", {"start": v(-72.92, -16.62) * mm, "end": v(-72.92, -16.97) * mm});
            skLineSegment(sketch, "E290", {"start": v(-72.92, -16.97) * mm, "end": v(-73.32, -17.1) * mm});
            skLineSegment(sketch, "E291", {"start": v(-73.32, -17.1) * mm, "end": v(-73.74, -17.14) * mm});
            skLineSegment(sketch, "E292", {"start": v(-73.74, -17.14) * mm, "end": v(-74.59, -16.83) * mm});
            skLineSegment(sketch, "E293", {"start": v(-74.59, -16.83) * mm, "end": v(-74.9, -15.99) * mm});
            skLineSegment(sketch, "E294", {"start": v(-74.9, -15.99) * mm, "end": v(-74.6, -15.12) * mm});
            skLineSegment(sketch, "E295", {"start": v(-74.6, -15.12) * mm, "end": v(-73.8, -14.8) * mm});
            skLineSegment(sketch, "E296", {"start": v(-73.8, -14.8) * mm, "end": v(-73.1, -15.09) * mm});
            skLineSegment(sketch, "E297", {"start": v(-73.1, -15.09) * mm, "end": v(-72.83, -15.87) * mm});
            skLineSegment(sketch, "E298", {"start": v(-73.2, -15.77) * mm, "end": v(-73.36, -15.28) * mm});
            skLineSegment(sketch, "E299", {"start": v(-73.36, -15.28) * mm, "end": v(-73.8, -15.1) * mm});
            skLineSegment(sketch, "E300", {"start": v(-73.8, -15.1) * mm, "end": v(-74.3, -15.28) * mm});
            skLineSegment(sketch, "E301", {"start": v(-74.3, -15.28) * mm, "end": v(-74.5, -15.77) * mm});
            skLineSegment(sketch, "E302", {"start": v(-74.5, -15.77) * mm, "end": v(-73.2, -15.77) * mm});
            skLineSegment(sketch, "E303", {"start": v(-70.93, -15.2) * mm, "end": v(-71.07, -15.14) * mm});
            skLineSegment(sketch, "E304", {"start": v(-71.07, -15.14) * mm, "end": v(-71.23, -15.12) * mm});
            skLineSegment(sketch, "E305", {"start": v(-71.23, -15.12) * mm, "end": v(-71.7, -15.32) * mm});
            skLineSegment(sketch, "E306", {"start": v(-71.7, -15.32) * mm, "end": v(-71.87, -15.9) * mm});
            skLineSegment(sketch, "E307", {"start": v(-71.87, -15.9) * mm, "end": v(-71.87, -17.08) * mm});
            skLineSegment(sketch, "E308", {"start": v(-71.87, -17.08) * mm, "end": v(-72.24, -17.08) * mm});
            skLineSegment(sketch, "E309", {"start": v(-72.24, -17.08) * mm, "end": v(-72.24, -14.85) * mm});
            skLineSegment(sketch, "E310", {"start": v(-72.24, -14.85) * mm, "end": v(-71.87, -14.85) * mm});
            skLineSegment(sketch, "E311", {"start": v(-71.87, -14.85) * mm, "end": v(-71.87, -15.2) * mm});
            skLineSegment(sketch, "E312", {"start": v(-71.87, -15.2) * mm, "end": v(-71.57, -14.9) * mm});
            skLineSegment(sketch, "E313", {"start": v(-71.57, -14.9) * mm, "end": v(-71.12, -14.8) * mm});
            skLineSegment(sketch, "E314", {"start": v(-71.12, -14.8) * mm, "end": v(-71.04, -14.8) * mm});
            skLineSegment(sketch, "E315", {"start": v(-71.04, -14.8) * mm, "end": v(-70.93, -14.81) * mm});
            skLineSegment(sketch, "E316", {"start": v(-70.93, -14.81) * mm, "end": v(-70.93, -15.2) * mm});
            skLineSegment(sketch, "E317", {"start": v(-90.44, 10.28) * mm, "end": v(-90.44, 9.88) * mm});
            skLineSegment(sketch, "E318", {"start": v(-90.44, 9.88) * mm, "end": v(-90.87, 10.05) * mm});
            skLineSegment(sketch, "E319", {"start": v(-90.87, 10.05) * mm, "end": v(-91.26, 10.1) * mm});
            skLineSegment(sketch, "E320", {"start": v(-91.26, 10.1) * mm, "end": v(-91.77, 9.98) * mm});
            skLineSegment(sketch, "E321", {"start": v(-91.77, 9.98) * mm, "end": v(-91.95, 9.61) * mm});
            skLineSegment(sketch, "E322", {"start": v(-91.95, 9.61) * mm, "end": v(-91.83, 9.31) * mm});
            skLineSegment(sketch, "E323", {"start": v(-91.83, 9.31) * mm, "end": v(-91.38, 9.15) * mm});
            skLineSegment(sketch, "E324", {"start": v(-91.38, 9.15) * mm, "end": v(-91.14, 9.1) * mm});
            skLineSegment(sketch, "E325", {"start": v(-91.14, 9.1) * mm, "end": v(-90.47, 8.8) * mm});
            skLineSegment(sketch, "E326", {"start": v(-90.47, 8.8) * mm, "end": v(-90.26, 8.22) * mm});
            skLineSegment(sketch, "E327", {"start": v(-90.26, 8.22) * mm, "end": v(-90.55, 7.56) * mm});
            skLineSegment(sketch, "E328", {"start": v(-90.55, 7.56) * mm, "end": v(-91.4, 7.34) * mm});
            skLineSegment(sketch, "E329", {"start": v(-91.4, 7.34) * mm, "end": v(-91.85, 7.39) * mm});
            skLineSegment(sketch, "E330", {"start": v(-91.85, 7.39) * mm, "end": v(-92.34, 7.53) * mm});
            skLineSegment(sketch, "E331", {"start": v(-92.34, 7.53) * mm, "end": v(-92.34, 7.95) * mm});
            skLineSegment(sketch, "E332", {"start": v(-92.34, 7.95) * mm, "end": v(-91.86, 7.74) * mm});
            skLineSegment(sketch, "E333", {"start": v(-91.86, 7.74) * mm, "end": v(-91.4, 7.67) * mm});
            skLineSegment(sketch, "E334", {"start": v(-91.4, 7.67) * mm, "end": v(-90.87, 7.8) * mm});
            skLineSegment(sketch, "E335", {"start": v(-90.87, 7.8) * mm, "end": v(-90.68, 8.2) * mm});
            skLineSegment(sketch, "E336", {"start": v(-90.68, 8.2) * mm, "end": v(-90.82, 8.53) * mm});
            skLineSegment(sketch, "E337", {"start": v(-90.82, 8.53) * mm, "end": v(-91.26, 8.72) * mm});
            skLineSegment(sketch, "E338", {"start": v(-91.26, 8.72) * mm, "end": v(-91.5, 8.77) * mm});
            skLineSegment(sketch, "E339", {"start": v(-91.5, 8.77) * mm, "end": v(-92.15, 9.05) * mm});
            skLineSegment(sketch, "E340", {"start": v(-92.15, 9.05) * mm, "end": v(-92.36, 9.58) * mm});
            skLineSegment(sketch, "E341", {"start": v(-92.36, 9.58) * mm, "end": v(-92.08, 10.2) * mm});
            skLineSegment(sketch, "E342", {"start": v(-92.08, 10.2) * mm, "end": v(-91.31, 10.43) * mm});
            skLineSegment(sketch, "E343", {"start": v(-91.31, 10.43) * mm, "end": v(-90.88, 10.4) * mm});
            skLineSegment(sketch, "E344", {"start": v(-90.88, 10.4) * mm, "end": v(-90.44, 10.28) * mm});
            skLineSegment(sketch, "E345", {"start": v(-87.8, 8.75) * mm, "end": v(-87.8, 7.4) * mm});
            skLineSegment(sketch, "E346", {"start": v(-87.8, 7.4) * mm, "end": v(-88.16, 7.4) * mm});
            skLineSegment(sketch, "E347", {"start": v(-88.16, 7.4) * mm, "end": v(-88.16, 8.74) * mm});
            skLineSegment(sketch, "E348", {"start": v(-88.16, 8.74) * mm, "end": v(-88.28, 9.2) * mm});
            skLineSegment(sketch, "E349", {"start": v(-88.28, 9.2) * mm, "end": v(-88.65, 9.37) * mm});
            skLineSegment(sketch, "E350", {"start": v(-88.65, 9.37) * mm, "end": v(-89.12, 9.18) * mm});
            skLineSegment(sketch, "E351", {"start": v(-89.12, 9.18) * mm, "end": v(-89.3, 8.66) * mm});
            skLineSegment(sketch, "E352", {"start": v(-89.3, 8.66) * mm, "end": v(-89.3, 7.4) * mm});
            skLineSegment(sketch, "E353", {"start": v(-89.3, 7.4) * mm, "end": v(-89.66, 7.4) * mm});
            skLineSegment(sketch, "E354", {"start": v(-89.66, 7.4) * mm, "end": v(-89.66, 10.5) * mm});
            skLineSegment(sketch, "E355", {"start": v(-89.66, 10.5) * mm, "end": v(-89.3, 10.5) * mm});
            skLineSegment(sketch, "E356", {"start": v(-89.3, 10.5) * mm, "end": v(-89.3, 9.29) * mm});
            skLineSegment(sketch, "E357", {"start": v(-89.3, 9.29) * mm, "end": v(-88.98, 9.59) * mm});
            skLineSegment(sketch, "E358", {"start": v(-88.98, 9.59) * mm, "end": v(-88.57, 9.69) * mm});
            skLineSegment(sketch, "E359", {"start": v(-88.57, 9.69) * mm, "end": v(-87.99, 9.45) * mm});
            skLineSegment(sketch, "E360", {"start": v(-87.99, 9.45) * mm, "end": v(-87.8, 8.75) * mm});
            skLineSegment(sketch, "E361", {"start": v(-87.1, 8.28) * mm, "end": v(-87.1, 9.63) * mm});
            skLineSegment(sketch, "E362", {"start": v(-87.1, 9.63) * mm, "end": v(-86.73, 9.63) * mm});
            skLineSegment(sketch, "E363", {"start": v(-86.73, 9.63) * mm, "end": v(-86.73, 8.3) * mm});
            skLineSegment(sketch, "E364", {"start": v(-86.73, 8.3) * mm, "end": v(-86.6, 7.82) * mm});
            skLineSegment(sketch, "E365", {"start": v(-86.6, 7.82) * mm, "end": v(-86.23, 7.66) * mm});
            skLineSegment(sketch, "E366", {"start": v(-86.23, 7.66) * mm, "end": v(-85.76, 7.85) * mm});
            skLineSegment(sketch, "E367", {"start": v(-85.76, 7.85) * mm, "end": v(-85.59, 8.37) * mm});
            skLineSegment(sketch, "E368", {"start": v(-85.59, 8.37) * mm, "end": v(-85.59, 9.63) * mm});
            skLineSegment(sketch, "E369", {"start": v(-85.59, 9.63) * mm, "end": v(-85.22, 9.63) * mm});
            skLineSegment(sketch, "E370", {"start": v(-85.22, 9.63) * mm, "end": v(-85.22, 7.4) * mm});
            skLineSegment(sketch, "E371", {"start": v(-85.22, 7.4) * mm, "end": v(-85.59, 7.4) * mm});
            skLineSegment(sketch, "E372", {"start": v(-85.59, 7.4) * mm, "end": v(-85.59, 7.74) * mm});
            skLineSegment(sketch, "E373", {"start": v(-85.59, 7.74) * mm, "end": v(-85.9, 7.44) * mm});
            skLineSegment(sketch, "E374", {"start": v(-85.9, 7.44) * mm, "end": v(-86.3, 7.34) * mm});
            skLineSegment(sketch, "E375", {"start": v(-86.3, 7.34) * mm, "end": v(-86.9, 7.58) * mm});
            skLineSegment(sketch, "E376", {"start": v(-86.9, 7.58) * mm, "end": v(-87.1, 8.28) * mm});
            skLineSegment(sketch, "E377", {"start": v(-84.1, 10.27) * mm, "end": v(-84.1, 9.63) * mm});
            skLineSegment(sketch, "E378", {"start": v(-84.1, 9.63) * mm, "end": v(-83.34, 9.63) * mm});
            skLineSegment(sketch, "E379", {"start": v(-83.34, 9.63) * mm, "end": v(-83.34, 9.35) * mm});
            skLineSegment(sketch, "E380", {"start": v(-83.34, 9.35) * mm, "end": v(-84.1, 9.35) * mm});
            skLineSegment(sketch, "E381", {"start": v(-84.1, 9.35) * mm, "end": v(-84.1, 8.13) * mm});
            skLineSegment(sketch, "E382", {"start": v(-84.1, 8.13) * mm, "end": v(-84.03, 7.78) * mm});
            skLineSegment(sketch, "E383", {"start": v(-84.03, 7.78) * mm, "end": v(-83.72, 7.7) * mm});
            skLineSegment(sketch, "E384", {"start": v(-83.72, 7.7) * mm, "end": v(-83.34, 7.7) * mm});
            skLineSegment(sketch, "E385", {"start": v(-83.34, 7.7) * mm, "end": v(-83.34, 7.4) * mm});
            skLineSegment(sketch, "E386", {"start": v(-83.34, 7.4) * mm, "end": v(-83.72, 7.4) * mm});
            skLineSegment(sketch, "E387", {"start": v(-83.72, 7.4) * mm, "end": v(-84.3, 7.56) * mm});
            skLineSegment(sketch, "E388", {"start": v(-84.3, 7.56) * mm, "end": v(-84.47, 8.13) * mm});
            skLineSegment(sketch, "E389", {"start": v(-84.47, 8.13) * mm, "end": v(-84.47, 9.35) * mm});
            skLineSegment(sketch, "E390", {"start": v(-84.47, 9.35) * mm, "end": v(-84.74, 9.35) * mm});
            skLineSegment(sketch, "E391", {"start": v(-84.74, 9.35) * mm, "end": v(-84.74, 9.63) * mm});
            skLineSegment(sketch, "E392", {"start": v(-84.74, 9.63) * mm, "end": v(-84.47, 9.63) * mm});
            skLineSegment(sketch, "E393", {"start": v(-84.47, 9.63) * mm, "end": v(-84.47, 10.27) * mm});
            skLineSegment(sketch, "E394", {"start": v(-84.47, 10.27) * mm, "end": v(-84.1, 10.27) * mm});
            skLineSegment(sketch, "E395", {"start": v(-82.5, 10.27) * mm, "end": v(-82.5, 9.63) * mm});
            skLineSegment(sketch, "E396", {"start": v(-82.5, 9.63) * mm, "end": v(-81.74, 9.63) * mm});
            skLineSegment(sketch, "E397", {"start": v(-81.74, 9.63) * mm, "end": v(-81.74, 9.35) * mm});
            skLineSegment(sketch, "E398", {"start": v(-81.74, 9.35) * mm, "end": v(-82.5, 9.35) * mm});
            skLineSegment(sketch, "E399", {"start": v(-82.5, 9.35) * mm, "end": v(-82.5, 8.13) * mm});
            skLineSegment(sketch, "E400", {"start": v(-82.5, 8.13) * mm, "end": v(-82.42, 7.78) * mm});
            skLineSegment(sketch, "E401", {"start": v(-82.42, 7.78) * mm, "end": v(-82.12, 7.7) * mm});
            skLineSegment(sketch, "E402", {"start": v(-82.12, 7.7) * mm, "end": v(-81.74, 7.7) * mm});
            skLineSegment(sketch, "E403", {"start": v(-81.74, 7.7) * mm, "end": v(-81.74, 7.4) * mm});
            skLineSegment(sketch, "E404", {"start": v(-81.74, 7.4) * mm, "end": v(-82.12, 7.4) * mm});
            skLineSegment(sketch, "E405", {"start": v(-82.12, 7.4) * mm, "end": v(-82.7, 7.56) * mm});
            skLineSegment(sketch, "E406", {"start": v(-82.7, 7.56) * mm, "end": v(-82.87, 8.13) * mm});
            skLineSegment(sketch, "E407", {"start": v(-82.87, 8.13) * mm, "end": v(-82.87, 9.35) * mm});
            skLineSegment(sketch, "E408", {"start": v(-82.87, 9.35) * mm, "end": v(-83.14, 9.35) * mm});
            skLineSegment(sketch, "E409", {"start": v(-83.14, 9.35) * mm, "end": v(-83.14, 9.63) * mm});
            skLineSegment(sketch, "E410", {"start": v(-83.14, 9.63) * mm, "end": v(-82.87, 9.63) * mm});
            skLineSegment(sketch, "E411", {"start": v(-82.87, 9.63) * mm, "end": v(-82.87, 10.27) * mm});
            skLineSegment(sketch, "E412", {"start": v(-82.87, 10.27) * mm, "end": v(-82.5, 10.27) * mm});
            skLineSegment(sketch, "E413", {"start": v(-79.35, 8.6) * mm, "end": v(-79.35, 8.43) * mm});
            skLineSegment(sketch, "E414", {"start": v(-79.35, 8.43) * mm, "end": v(-81.03, 8.43) * mm});
            skLineSegment(sketch, "E415", {"start": v(-81.03, 8.43) * mm, "end": v(-80.8, 7.85) * mm});
            skLineSegment(sketch, "E416", {"start": v(-80.8, 7.85) * mm, "end": v(-80.24, 7.65) * mm});
            skLineSegment(sketch, "E417", {"start": v(-80.24, 7.65) * mm, "end": v(-79.83, 7.7) * mm});
            skLineSegment(sketch, "E418", {"start": v(-79.83, 7.7) * mm, "end": v(-79.43, 7.86) * mm});
            skLineSegment(sketch, "E419", {"start": v(-79.43, 7.86) * mm, "end": v(-79.43, 7.51) * mm});
            skLineSegment(sketch, "E420", {"start": v(-79.43, 7.51) * mm, "end": v(-79.84, 7.38) * mm});
            skLineSegment(sketch, "E421", {"start": v(-79.84, 7.38) * mm, "end": v(-80.26, 7.34) * mm});
            skLineSegment(sketch, "E422", {"start": v(-80.26, 7.34) * mm, "end": v(-81.1, 7.65) * mm});
            skLineSegment(sketch, "E423", {"start": v(-81.1, 7.65) * mm, "end": v(-81.42, 8.5) * mm});
            skLineSegment(sketch, "E424", {"start": v(-81.42, 8.5) * mm, "end": v(-81.12, 9.36) * mm});
            skLineSegment(sketch, "E425", {"start": v(-81.12, 9.36) * mm, "end": v(-80.32, 9.69) * mm});
            skLineSegment(sketch, "E426", {"start": v(-80.32, 9.69) * mm, "end": v(-79.61, 9.4) * mm});
            skLineSegment(sketch, "E427", {"start": v(-79.61, 9.4) * mm, "end": v(-79.35, 8.6) * mm});
            skLineSegment(sketch, "E428", {"start": v(-79.71, 8.72) * mm, "end": v(-79.88, 9.2) * mm});
            skLineSegment(sketch, "E429", {"start": v(-79.88, 9.2) * mm, "end": v(-80.32, 9.37) * mm});
            skLineSegment(sketch, "E430", {"start": v(-80.32, 9.37) * mm, "end": v(-80.81, 9.2) * mm});
            skLineSegment(sketch, "E431", {"start": v(-80.81, 9.2) * mm, "end": v(-81.02, 8.71) * mm});
            skLineSegment(sketch, "E432", {"start": v(-81.02, 8.71) * mm, "end": v(-79.71, 8.72) * mm});
            skLineSegment(sketch, "E433", {"start": v(-77.45, 9.29) * mm, "end": v(-77.59, 9.34) * mm});
            skLineSegment(sketch, "E434", {"start": v(-77.59, 9.34) * mm, "end": v(-77.75, 9.36) * mm});
            skLineSegment(sketch, "E435", {"start": v(-77.75, 9.36) * mm, "end": v(-78.22, 9.16) * mm});
            skLineSegment(sketch, "E436", {"start": v(-78.22, 9.16) * mm, "end": v(-78.4, 8.58) * mm});
            skLineSegment(sketch, "E437", {"start": v(-78.4, 8.58) * mm, "end": v(-78.4, 7.4) * mm});
            skLineSegment(sketch, "E438", {"start": v(-78.4, 7.4) * mm, "end": v(-78.76, 7.4) * mm});
            skLineSegment(sketch, "E439", {"start": v(-78.76, 7.4) * mm, "end": v(-78.76, 9.63) * mm});
            skLineSegment(sketch, "E440", {"start": v(-78.76, 9.63) * mm, "end": v(-78.4, 9.63) * mm});
            skLineSegment(sketch, "E441", {"start": v(-78.4, 9.63) * mm, "end": v(-78.4, 9.29) * mm});
            skLineSegment(sketch, "E442", {"start": v(-78.4, 9.29) * mm, "end": v(-78.09, 9.59) * mm});
            skLineSegment(sketch, "E443", {"start": v(-78.09, 9.59) * mm, "end": v(-77.64, 9.69) * mm});
            skLineSegment(sketch, "E444", {"start": v(-77.64, 9.69) * mm, "end": v(-77.55, 9.68) * mm});
            skLineSegment(sketch, "E445", {"start": v(-77.55, 9.68) * mm, "end": v(-77.45, 9.67) * mm});
            skLineSegment(sketch, "E446", {"start": v(-77.45, 9.67) * mm, "end": v(-77.45, 9.29) * mm});
            skLineSegment(sketch, "E447", {"start": v(-55.42, -10.02) * mm, "end": v(-55.42, -10.45) * mm});
            skLineSegment(sketch, "E448", {"start": v(-55.42, -10.45) * mm, "end": v(-55.86, -10.16) * mm});
            skLineSegment(sketch, "E449", {"start": v(-55.86, -10.16) * mm, "end": v(-56.35, -10.07) * mm});
            skLineSegment(sketch, "E450", {"start": v(-56.35, -10.07) * mm, "end": v(-57.13, -10.38) * mm});
            skLineSegment(sketch, "E451", {"start": v(-57.13, -10.38) * mm, "end": v(-57.4, -11.28) * mm});
            skLineSegment(sketch, "E452", {"start": v(-57.4, -11.28) * mm, "end": v(-57.13, -12.19) * mm});
            skLineSegment(sketch, "E453", {"start": v(-57.13, -12.19) * mm, "end": v(-56.35, -12.5) * mm});
            skLineSegment(sketch, "E454", {"start": v(-56.35, -12.5) * mm, "end": v(-55.86, -12.4) * mm});
            skLineSegment(sketch, "E455", {"start": v(-55.86, -12.4) * mm, "end": v(-55.42, -12.12) * mm});
            skLineSegment(sketch, "E456", {"start": v(-55.42, -12.12) * mm, "end": v(-55.42, -12.54) * mm});
            skLineSegment(sketch, "E457", {"start": v(-55.42, -12.54) * mm, "end": v(-55.87, -12.76) * mm});
            skLineSegment(sketch, "E458", {"start": v(-55.87, -12.76) * mm, "end": v(-56.37, -12.83) * mm});
            skLineSegment(sketch, "E459", {"start": v(-56.37, -12.83) * mm, "end": v(-56.98, -12.72) * mm});
            skLineSegment(sketch, "E460", {"start": v(-56.98, -12.72) * mm, "end": v(-57.44, -12.41) * mm});
            skLineSegment(sketch, "E461", {"start": v(-57.44, -12.41) * mm, "end": v(-57.73, -11.92) * mm});
            skLineSegment(sketch, "E462", {"start": v(-57.73, -11.92) * mm, "end": v(-57.82, -11.28) * mm});
            skLineSegment(sketch, "E463", {"start": v(-57.82, -11.28) * mm, "end": v(-57.73, -10.64) * mm});
            skLineSegment(sketch, "E464", {"start": v(-57.73, -10.64) * mm, "end": v(-57.44, -10.15) * mm});
            skLineSegment(sketch, "E465", {"start": v(-57.44, -10.15) * mm, "end": v(-56.98, -9.84) * mm});
            skLineSegment(sketch, "E466", {"start": v(-56.98, -9.84) * mm, "end": v(-56.37, -9.74) * mm});
            skLineSegment(sketch, "E467", {"start": v(-56.37, -9.74) * mm, "end": v(-55.87, -9.8) * mm});
            skLineSegment(sketch, "E468", {"start": v(-55.87, -9.8) * mm, "end": v(-55.42, -10.02) * mm});
            skLineSegment(sketch, "E469", {"start": v(-53.8, -11.65) * mm, "end": v(-54.42, -11.75) * mm});
            skLineSegment(sketch, "E470", {"start": v(-54.42, -11.75) * mm, "end": v(-54.59, -12.1) * mm});
            skLineSegment(sketch, "E471", {"start": v(-54.59, -12.1) * mm, "end": v(-54.46, -12.4) * mm});
            skLineSegment(sketch, "E472", {"start": v(-54.46, -12.4) * mm, "end": v(-54.1, -12.52) * mm});
            skLineSegment(sketch, "E473", {"start": v(-54.1, -12.52) * mm, "end": v(-53.62, -12.3) * mm});
            skLineSegment(sketch, "E474", {"start": v(-53.62, -12.3) * mm, "end": v(-53.43, -11.73) * mm});
            skLineSegment(sketch, "E475", {"start": v(-53.43, -11.73) * mm, "end": v(-53.43, -11.65) * mm});
            skLineSegment(sketch, "E476", {"start": v(-53.43, -11.65) * mm, "end": v(-53.8, -11.65) * mm});
            skLineSegment(sketch, "E477", {"start": v(-53.07, -11.5) * mm, "end": v(-53.07, -12.77) * mm});
            skLineSegment(sketch, "E478", {"start": v(-53.07, -12.77) * mm, "end": v(-53.43, -12.77) * mm});
            skLineSegment(sketch, "E479", {"start": v(-53.43, -12.77) * mm, "end": v(-53.43, -12.43) * mm});
            skLineSegment(sketch, "E480", {"start": v(-53.43, -12.43) * mm, "end": v(-53.75, -12.73) * mm});
            skLineSegment(sketch, "E481", {"start": v(-53.75, -12.73) * mm, "end": v(-54.2, -12.83) * mm});
            skLineSegment(sketch, "E482", {"start": v(-54.2, -12.83) * mm, "end": v(-54.75, -12.64) * mm});
            skLineSegment(sketch, "E483", {"start": v(-54.75, -12.64) * mm, "end": v(-54.95, -12.12) * mm});
            skLineSegment(sketch, "E484", {"start": v(-54.95, -12.12) * mm, "end": v(-54.7, -11.55) * mm});
            skLineSegment(sketch, "E485", {"start": v(-54.7, -11.55) * mm, "end": v(-53.95, -11.36) * mm});
            skLineSegment(sketch, "E486", {"start": v(-53.95, -11.36) * mm, "end": v(-53.43, -11.36) * mm});
            skLineSegment(sketch, "E487", {"start": v(-53.43, -11.36) * mm, "end": v(-53.43, -11.32) * mm});
            skLineSegment(sketch, "E488", {"start": v(-53.43, -11.32) * mm, "end": v(-53.6, -10.93) * mm});
            skLineSegment(sketch, "E489", {"start": v(-53.6, -10.93) * mm, "end": v(-54.07, -10.8) * mm});
            skLineSegment(sketch, "E490", {"start": v(-54.07, -10.8) * mm, "end": v(-54.44, -10.84) * mm});
            skLineSegment(sketch, "E491", {"start": v(-54.44, -10.84) * mm, "end": v(-54.8, -10.98) * mm});
            skLineSegment(sketch, "E492", {"start": v(-54.8, -10.98) * mm, "end": v(-54.8, -10.64) * mm});
            skLineSegment(sketch, "E493", {"start": v(-54.8, -10.64) * mm, "end": v(-54.4, -10.52) * mm});
            skLineSegment(sketch, "E494", {"start": v(-54.4, -10.52) * mm, "end": v(-54.03, -10.48) * mm});
            skLineSegment(sketch, "E495", {"start": v(-54.03, -10.48) * mm, "end": v(-53.3, -10.73) * mm});
            skLineSegment(sketch, "E496", {"start": v(-53.3, -10.73) * mm, "end": v(-53.07, -11.5) * mm});
            skLineSegment(sketch, "E497", {"start": v(-50.57, -10.97) * mm, "end": v(-50.24, -10.6) * mm});
            skLineSegment(sketch, "E498", {"start": v(-50.24, -10.6) * mm, "end": v(-49.8, -10.48) * mm});
            skLineSegment(sketch, "E499", {"start": v(-49.8, -10.48) * mm, "end": v(-49.25, -10.73) * mm});
            skLineSegment(sketch, "E500", {"start": v(-49.25, -10.73) * mm, "end": v(-49.06, -11.42) * mm});
            skLineSegment(sketch, "E501", {"start": v(-49.06, -11.42) * mm, "end": v(-49.06, -12.77) * mm});
            skLineSegment(sketch, "E502", {"start": v(-49.06, -12.77) * mm, "end": v(-49.43, -12.77) * mm});
            skLineSegment(sketch, "E503", {"start": v(-49.43, -12.77) * mm, "end": v(-49.43, -11.43) * mm});
            skLineSegment(sketch, "E504", {"start": v(-49.43, -11.43) * mm, "end": v(-49.55, -10.96) * mm});
            skLineSegment(sketch, "E505", {"start": v(-49.55, -10.96) * mm, "end": v(-49.9, -10.8) * mm});
            skLineSegment(sketch, "E506", {"start": v(-49.9, -10.8) * mm, "end": v(-50.34, -11) * mm});
            skLineSegment(sketch, "E507", {"start": v(-50.34, -11) * mm, "end": v(-50.51, -11.5) * mm});
            skLineSegment(sketch, "E508", {"start": v(-50.51, -11.5) * mm, "end": v(-50.51, -12.77) * mm});
            skLineSegment(sketch, "E509", {"start": v(-50.51, -12.77) * mm, "end": v(-50.88, -12.77) * mm});
            skLineSegment(sketch, "E510", {"start": v(-50.88, -12.77) * mm, "end": v(-50.88, -11.43) * mm});
            skLineSegment(sketch, "E511", {"start": v(-50.88, -11.43) * mm, "end": v(-51, -10.96) * mm});
            skLineSegment(sketch, "E512", {"start": v(-51, -10.96) * mm, "end": v(-51.34, -10.8) * mm});
            skLineSegment(sketch, "E513", {"start": v(-51.34, -10.8) * mm, "end": v(-51.8, -11) * mm});
            skLineSegment(sketch, "E514", {"start": v(-51.8, -11) * mm, "end": v(-51.95, -11.5) * mm});
            skLineSegment(sketch, "E515", {"start": v(-51.95, -11.5) * mm, "end": v(-51.95, -12.77) * mm});
            skLineSegment(sketch, "E516", {"start": v(-51.95, -12.77) * mm, "end": v(-52.32, -12.77) * mm});
            skLineSegment(sketch, "E517", {"start": v(-52.32, -12.77) * mm, "end": v(-52.32, -10.54) * mm});
            skLineSegment(sketch, "E518", {"start": v(-52.32, -10.54) * mm, "end": v(-51.95, -10.54) * mm});
            skLineSegment(sketch, "E519", {"start": v(-51.95, -10.54) * mm, "end": v(-51.95, -10.88) * mm});
            skLineSegment(sketch, "E520", {"start": v(-51.95, -10.88) * mm, "end": v(-51.65, -10.58) * mm});
            skLineSegment(sketch, "E521", {"start": v(-51.65, -10.58) * mm, "end": v(-51.24, -10.48) * mm});
            skLineSegment(sketch, "E522", {"start": v(-51.24, -10.48) * mm, "end": v(-50.83, -10.6) * mm});
            skLineSegment(sketch, "E523", {"start": v(-50.83, -10.6) * mm, "end": v(-50.57, -10.97) * mm});
            skLineSegment(sketch, "E524", {"start": v(-46.42, -11.56) * mm, "end": v(-46.42, -11.74) * mm});
            skLineSegment(sketch, "E525", {"start": v(-46.42, -11.74) * mm, "end": v(-48.1, -11.74) * mm});
            skLineSegment(sketch, "E526", {"start": v(-48.1, -11.74) * mm, "end": v(-47.88, -12.32) * mm});
            skLineSegment(sketch, "E527", {"start": v(-47.88, -12.32) * mm, "end": v(-47.3, -12.52) * mm});
            skLineSegment(sketch, "E528", {"start": v(-47.3, -12.52) * mm, "end": v(-46.9, -12.46) * mm});
            skLineSegment(sketch, "E529", {"start": v(-46.9, -12.46) * mm, "end": v(-46.5, -12.3) * mm});
            skLineSegment(sketch, "E530", {"start": v(-46.5, -12.3) * mm, "end": v(-46.5, -12.66) * mm});
            skLineSegment(sketch, "E531", {"start": v(-46.5, -12.66) * mm, "end": v(-46.91, -12.78) * mm});
            skLineSegment(sketch, "E532", {"start": v(-46.91, -12.78) * mm, "end": v(-47.33, -12.83) * mm});
            skLineSegment(sketch, "E533", {"start": v(-47.33, -12.83) * mm, "end": v(-48.18, -12.52) * mm});
            skLineSegment(sketch, "E534", {"start": v(-48.18, -12.52) * mm, "end": v(-48.49, -11.67) * mm});
            skLineSegment(sketch, "E535", {"start": v(-48.49, -11.67) * mm, "end": v(-48.2, -10.8) * mm});
            skLineSegment(sketch, "E536", {"start": v(-48.2, -10.8) * mm, "end": v(-47.4, -10.48) * mm});
            skLineSegment(sketch, "E537", {"start": v(-47.4, -10.48) * mm, "end": v(-46.68, -10.77) * mm});
            skLineSegment(sketch, "E538", {"start": v(-46.68, -10.77) * mm, "end": v(-46.42, -11.56) * mm});
            skLineSegment(sketch, "E539", {"start": v(-46.79, -11.45) * mm, "end": v(-46.96, -10.97) * mm});
            skLineSegment(sketch, "E540", {"start": v(-46.96, -10.97) * mm, "end": v(-47.4, -10.8) * mm});
            skLineSegment(sketch, "E541", {"start": v(-47.4, -10.8) * mm, "end": v(-47.88, -10.97) * mm});
            skLineSegment(sketch, "E542", {"start": v(-47.88, -10.97) * mm, "end": v(-48.1, -11.46) * mm});
            skLineSegment(sketch, "E543", {"start": v(-48.1, -11.46) * mm, "end": v(-46.79, -11.45) * mm});
            skLineSegment(sketch, "E544", {"start": v(-44.52, -10.88) * mm, "end": v(-44.66, -10.83) * mm});
            skLineSegment(sketch, "E545", {"start": v(-44.66, -10.83) * mm, "end": v(-44.82, -10.8) * mm});
            skLineSegment(sketch, "E546", {"start": v(-44.82, -10.8) * mm, "end": v(-45.3, -11.01) * mm});
            skLineSegment(sketch, "E547", {"start": v(-45.3, -11.01) * mm, "end": v(-45.46, -11.6) * mm});
            skLineSegment(sketch, "E548", {"start": v(-45.46, -11.6) * mm, "end": v(-45.46, -12.77) * mm});
            skLineSegment(sketch, "E549", {"start": v(-45.46, -12.77) * mm, "end": v(-45.83, -12.77) * mm});
            skLineSegment(sketch, "E550", {"start": v(-45.83, -12.77) * mm, "end": v(-45.83, -10.54) * mm});
            skLineSegment(sketch, "E551", {"start": v(-45.83, -10.54) * mm, "end": v(-45.46, -10.54) * mm});
            skLineSegment(sketch, "E552", {"start": v(-45.46, -10.54) * mm, "end": v(-45.46, -10.88) * mm});
            skLineSegment(sketch, "E553", {"start": v(-45.46, -10.88) * mm, "end": v(-45.16, -10.58) * mm});
            skLineSegment(sketch, "E554", {"start": v(-45.16, -10.58) * mm, "end": v(-44.71, -10.48) * mm});
            skLineSegment(sketch, "E555", {"start": v(-44.71, -10.48) * mm, "end": v(-44.63, -10.49) * mm});
            skLineSegment(sketch, "E556", {"start": v(-44.63, -10.49) * mm, "end": v(-44.53, -10.5) * mm});
            skLineSegment(sketch, "E557", {"start": v(-44.53, -10.5) * mm, "end": v(-44.52, -10.88) * mm});
            skLineSegment(sketch, "E558", {"start": v(-43.12, -11.65) * mm, "end": v(-43.74, -11.75) * mm});
            skLineSegment(sketch, "E559", {"start": v(-43.74, -11.75) * mm, "end": v(-43.9, -12.1) * mm});
            skLineSegment(sketch, "E560", {"start": v(-43.9, -12.1) * mm, "end": v(-43.78, -12.4) * mm});
            skLineSegment(sketch, "E561", {"start": v(-43.78, -12.4) * mm, "end": v(-43.43, -12.52) * mm});
            skLineSegment(sketch, "E562", {"start": v(-43.43, -12.52) * mm, "end": v(-42.94, -12.3) * mm});
            skLineSegment(sketch, "E563", {"start": v(-42.94, -12.3) * mm, "end": v(-42.76, -11.73) * mm});
            skLineSegment(sketch, "E564", {"start": v(-42.76, -11.73) * mm, "end": v(-42.76, -11.65) * mm});
            skLineSegment(sketch, "E565", {"start": v(-42.76, -11.65) * mm, "end": v(-43.12, -11.65) * mm});
            skLineSegment(sketch, "E566", {"start": v(-42.39, -11.5) * mm, "end": v(-42.39, -12.77) * mm});
            skLineSegment(sketch, "E567", {"start": v(-42.39, -12.77) * mm, "end": v(-42.76, -12.77) * mm});
            skLineSegment(sketch, "E568", {"start": v(-42.76, -12.77) * mm, "end": v(-42.76, -12.43) * mm});
            skLineSegment(sketch, "E569", {"start": v(-42.76, -12.43) * mm, "end": v(-43.07, -12.73) * mm});
            skLineSegment(sketch, "E570", {"start": v(-43.07, -12.73) * mm, "end": v(-43.53, -12.83) * mm});
            skLineSegment(sketch, "E571", {"start": v(-43.53, -12.83) * mm, "end": v(-44.07, -12.64) * mm});
            skLineSegment(sketch, "E572", {"start": v(-44.07, -12.64) * mm, "end": v(-44.27, -12.12) * mm});
            skLineSegment(sketch, "E573", {"start": v(-44.27, -12.12) * mm, "end": v(-44.02, -11.55) * mm});
            skLineSegment(sketch, "E574", {"start": v(-44.02, -11.55) * mm, "end": v(-43.27, -11.36) * mm});
            skLineSegment(sketch, "E575", {"start": v(-43.27, -11.36) * mm, "end": v(-42.76, -11.36) * mm});
            skLineSegment(sketch, "E576", {"start": v(-42.76, -11.36) * mm, "end": v(-42.76, -11.32) * mm});
            skLineSegment(sketch, "E577", {"start": v(-42.76, -11.32) * mm, "end": v(-42.92, -10.93) * mm});
            skLineSegment(sketch, "E578", {"start": v(-42.92, -10.93) * mm, "end": v(-43.39, -10.8) * mm});
            skLineSegment(sketch, "E579", {"start": v(-43.39, -10.8) * mm, "end": v(-43.76, -10.84) * mm});
            skLineSegment(sketch, "E580", {"start": v(-43.76, -10.84) * mm, "end": v(-44.11, -10.98) * mm});
            skLineSegment(sketch, "E581", {"start": v(-44.11, -10.98) * mm, "end": v(-44.11, -10.64) * mm});
            skLineSegment(sketch, "E582", {"start": v(-44.11, -10.64) * mm, "end": v(-43.72, -10.52) * mm});
            skLineSegment(sketch, "E583", {"start": v(-43.72, -10.52) * mm, "end": v(-43.35, -10.48) * mm});
            skLineSegment(sketch, "E584", {"start": v(-43.35, -10.48) * mm, "end": v(-42.63, -10.73) * mm});
            skLineSegment(sketch, "E585", {"start": v(-42.63, -10.73) * mm, "end": v(-42.39, -11.5) * mm});
            skLineSegment(sketch, "E586", {"start": v(-53.87, -14.9) * mm, "end": v(-53.47, -14.9) * mm});
            skLineSegment(sketch, "E587", {"start": v(-53.47, -14.9) * mm, "end": v(-53.47, -16.7) * mm});
            skLineSegment(sketch, "E588", {"start": v(-53.47, -16.7) * mm, "end": v(-53.3, -17.4) * mm});
            skLineSegment(sketch, "E589", {"start": v(-53.3, -17.4) * mm, "end": v(-52.73, -17.6) * mm});
            skLineSegment(sketch, "E590", {"start": v(-52.73, -17.6) * mm, "end": v(-52.17, -17.4) * mm});
            skLineSegment(sketch, "E591", {"start": v(-52.17, -17.4) * mm, "end": v(-52, -16.7) * mm});
            skLineSegment(sketch, "E592", {"start": v(-52, -16.7) * mm, "end": v(-52, -14.9) * mm});
            skLineSegment(sketch, "E593", {"start": v(-52, -14.9) * mm, "end": v(-51.6, -14.9) * mm});
            skLineSegment(sketch, "E594", {"start": v(-51.6, -14.9) * mm, "end": v(-51.6, -16.76) * mm});
            skLineSegment(sketch, "E595", {"start": v(-51.6, -16.76) * mm, "end": v(-51.88, -17.63) * mm});
            skLineSegment(sketch, "E596", {"start": v(-51.88, -17.63) * mm, "end": v(-52.73, -17.93) * mm});
            skLineSegment(sketch, "E597", {"start": v(-52.73, -17.93) * mm, "end": v(-53.58, -17.63) * mm});
            skLineSegment(sketch, "E598", {"start": v(-53.58, -17.63) * mm, "end": v(-53.87, -16.76) * mm});
            skLineSegment(sketch, "E599", {"start": v(-53.87, -16.76) * mm, "end": v(-53.87, -14.9) * mm});
            skLineSegment(sketch, "E600", {"start": v(-49.05, -15) * mm, "end": v(-49.05, -15.39) * mm});
            skLineSegment(sketch, "E601", {"start": v(-49.05, -15.39) * mm, "end": v(-49.48, -15.22) * mm});
            skLineSegment(sketch, "E602", {"start": v(-49.48, -15.22) * mm, "end": v(-49.88, -15.17) * mm});
            skLineSegment(sketch, "E603", {"start": v(-49.88, -15.17) * mm, "end": v(-50.38, -15.3) * mm});
            skLineSegment(sketch, "E604", {"start": v(-50.38, -15.3) * mm, "end": v(-50.56, -15.66) * mm});
            skLineSegment(sketch, "E605", {"start": v(-50.56, -15.66) * mm, "end": v(-50.44, -15.96) * mm});
            skLineSegment(sketch, "E606", {"start": v(-50.44, -15.96) * mm, "end": v(-50, -16.12) * mm});
            skLineSegment(sketch, "E607", {"start": v(-50, -16.12) * mm, "end": v(-49.75, -16.17) * mm});
            skLineSegment(sketch, "E608", {"start": v(-49.75, -16.17) * mm, "end": v(-49.09, -16.47) * mm});
            skLineSegment(sketch, "E609", {"start": v(-49.09, -16.47) * mm, "end": v(-48.87, -17.05) * mm});
            skLineSegment(sketch, "E610", {"start": v(-48.87, -17.05) * mm, "end": v(-49.16, -17.7) * mm});
            skLineSegment(sketch, "E611", {"start": v(-49.16, -17.7) * mm, "end": v(-50.01, -17.93) * mm});
            skLineSegment(sketch, "E612", {"start": v(-50.01, -17.93) * mm, "end": v(-50.46, -17.88) * mm});
            skLineSegment(sketch, "E613", {"start": v(-50.46, -17.88) * mm, "end": v(-50.95, -17.74) * mm});
            skLineSegment(sketch, "E614", {"start": v(-50.95, -17.74) * mm, "end": v(-50.95, -17.33) * mm});
            skLineSegment(sketch, "E615", {"start": v(-50.95, -17.33) * mm, "end": v(-50.47, -17.53) * mm});
            skLineSegment(sketch, "E616", {"start": v(-50.47, -17.53) * mm, "end": v(-50.01, -17.6) * mm});
            skLineSegment(sketch, "E617", {"start": v(-50.01, -17.6) * mm, "end": v(-49.48, -17.47) * mm});
            skLineSegment(sketch, "E618", {"start": v(-49.48, -17.47) * mm, "end": v(-49.3, -17.08) * mm});
            skLineSegment(sketch, "E619", {"start": v(-49.3, -17.08) * mm, "end": v(-49.43, -16.74) * mm});
            skLineSegment(sketch, "E620", {"start": v(-49.43, -16.74) * mm, "end": v(-49.87, -16.55) * mm});
            skLineSegment(sketch, "E621", {"start": v(-49.87, -16.55) * mm, "end": v(-50.11, -16.5) * mm});
            skLineSegment(sketch, "E622", {"start": v(-50.11, -16.5) * mm, "end": v(-50.77, -16.22) * mm});
            skLineSegment(sketch, "E623", {"start": v(-50.77, -16.22) * mm, "end": v(-50.97, -15.7) * mm});
            skLineSegment(sketch, "E624", {"start": v(-50.97, -15.7) * mm, "end": v(-50.69, -15.07) * mm});
            skLineSegment(sketch, "E625", {"start": v(-50.69, -15.07) * mm, "end": v(-49.92, -14.84) * mm});
            skLineSegment(sketch, "E626", {"start": v(-49.92, -14.84) * mm, "end": v(-49.5, -14.88) * mm});
            skLineSegment(sketch, "E627", {"start": v(-49.5, -14.88) * mm, "end": v(-49.05, -15) * mm});
            skLineSegment(sketch, "E628", {"start": v(-47.84, -16.45) * mm, "end": v(-47.84, -17.54) * mm});
            skLineSegment(sketch, "E629", {"start": v(-47.84, -17.54) * mm, "end": v(-47.2, -17.54) * mm});
            skLineSegment(sketch, "E630", {"start": v(-47.2, -17.54) * mm, "end": v(-46.71, -17.4) * mm});
            skLineSegment(sketch, "E631", {"start": v(-46.71, -17.4) * mm, "end": v(-46.56, -17) * mm});
            skLineSegment(sketch, "E632", {"start": v(-46.56, -17) * mm, "end": v(-46.71, -16.58) * mm});
            skLineSegment(sketch, "E633", {"start": v(-46.71, -16.58) * mm, "end": v(-47.2, -16.45) * mm});
            skLineSegment(sketch, "E634", {"start": v(-47.2, -16.45) * mm, "end": v(-47.84, -16.45) * mm});
            skLineSegment(sketch, "E635", {"start": v(-47.84, -15.23) * mm, "end": v(-47.84, -16.13) * mm});
            skLineSegment(sketch, "E636", {"start": v(-47.84, -16.13) * mm, "end": v(-47.24, -16.13) * mm});
            skLineSegment(sketch, "E637", {"start": v(-47.24, -16.13) * mm, "end": v(-46.8, -16.01) * mm});
            skLineSegment(sketch, "E638", {"start": v(-46.8, -16.01) * mm, "end": v(-46.66, -15.68) * mm});
            skLineSegment(sketch, "E639", {"start": v(-46.66, -15.68) * mm, "end": v(-46.8, -15.34) * mm});
            skLineSegment(sketch, "E640", {"start": v(-46.8, -15.34) * mm, "end": v(-47.24, -15.23) * mm});
            skLineSegment(sketch, "E641", {"start": v(-47.24, -15.23) * mm, "end": v(-47.84, -15.23) * mm});
            skLineSegment(sketch, "E642", {"start": v(-48.24, -14.9) * mm, "end": v(-47.21, -14.9) * mm});
            skLineSegment(sketch, "E643", {"start": v(-47.21, -14.9) * mm, "end": v(-46.5, -15.09) * mm});
            skLineSegment(sketch, "E644", {"start": v(-46.5, -15.09) * mm, "end": v(-46.26, -15.63) * mm});
            skLineSegment(sketch, "E645", {"start": v(-46.26, -15.63) * mm, "end": v(-46.38, -16.07) * mm});
            skLineSegment(sketch, "E646", {"start": v(-46.38, -16.07) * mm, "end": v(-46.76, -16.27) * mm});
            skLineSegment(sketch, "E647", {"start": v(-46.76, -16.27) * mm, "end": v(-46.3, -16.54) * mm});
            skLineSegment(sketch, "E648", {"start": v(-46.3, -16.54) * mm, "end": v(-46.13, -17.04) * mm});
            skLineSegment(sketch, "E649", {"start": v(-46.13, -17.04) * mm, "end": v(-46.4, -17.66) * mm});
            skLineSegment(sketch, "E650", {"start": v(-46.4, -17.66) * mm, "end": v(-47.17, -17.87) * mm});
            skLineSegment(sketch, "E651", {"start": v(-47.17, -17.87) * mm, "end": v(-48.24, -17.87) * mm});
            skLineSegment(sketch, "E652", {"start": v(-48.24, -17.87) * mm, "end": v(-48.24, -14.9) * mm});
            skLineSegment(sketch, "E653", {"start": v(-98.71, 16.09) * mm, "end": v(-98.05, 16.09) * mm});
            skLineSegment(sketch, "E654", {"start": v(-98.05, 16.09) * mm, "end": v(-98.05, 18.36) * mm});
            skLineSegment(sketch, "E655", {"start": v(-98.05, 18.36) * mm, "end": v(-98.77, 18.22) * mm});
            skLineSegment(sketch, "E656", {"start": v(-98.77, 18.22) * mm, "end": v(-98.77, 18.58) * mm});
            skLineSegment(sketch, "E657", {"start": v(-98.77, 18.58) * mm, "end": v(-98.06, 18.73) * mm});
            skLineSegment(sketch, "E658", {"start": v(-98.06, 18.73) * mm, "end": v(-97.66, 18.73) * mm});
            skLineSegment(sketch, "E659", {"start": v(-97.66, 18.73) * mm, "end": v(-97.66, 16.09) * mm});
            skLineSegment(sketch, "E660", {"start": v(-97.66, 16.09) * mm, "end": v(-97, 16.09) * mm});
            skLineSegment(sketch, "E661", {"start": v(-97, 16.09) * mm, "end": v(-97, 15.75) * mm});
            skLineSegment(sketch, "E662", {"start": v(-97, 15.75) * mm, "end": v(-98.71, 15.75) * mm});
            skLineSegment(sketch, "E663", {"start": v(-98.71, 15.75) * mm, "end": v(-98.71, 16.09) * mm});
            skLineSegment(sketch, "E664", {"start": v(-89.97, 16.06) * mm, "end": v(-88.57, 16.06) * mm});
            skLineSegment(sketch, "E665", {"start": v(-88.57, 16.06) * mm, "end": v(-88.57, 15.72) * mm});
            skLineSegment(sketch, "E666", {"start": v(-88.57, 15.72) * mm, "end": v(-90.46, 15.72) * mm});
            skLineSegment(sketch, "E667", {"start": v(-90.46, 15.72) * mm, "end": v(-90.46, 16.06) * mm});
            skLineSegment(sketch, "E668", {"start": v(-90.46, 16.06) * mm, "end": v(-89.83, 16.7) * mm});
            skLineSegment(sketch, "E669", {"start": v(-89.83, 16.7) * mm, "end": v(-89.34, 17.22) * mm});
            skLineSegment(sketch, "E670", {"start": v(-89.34, 17.22) * mm, "end": v(-89.07, 17.58) * mm});
            skLineSegment(sketch, "E671", {"start": v(-89.07, 17.58) * mm, "end": v(-88.99, 17.88) * mm});
            skLineSegment(sketch, "E672", {"start": v(-88.99, 17.88) * mm, "end": v(-89.16, 18.27) * mm});
            skLineSegment(sketch, "E673", {"start": v(-89.16, 18.27) * mm, "end": v(-89.6, 18.42) * mm});
            skLineSegment(sketch, "E674", {"start": v(-89.6, 18.42) * mm, "end": v(-90, 18.35) * mm});
            skLineSegment(sketch, "E675", {"start": v(-90, 18.35) * mm, "end": v(-90.44, 18.15) * mm});
            skLineSegment(sketch, "E676", {"start": v(-90.44, 18.15) * mm, "end": v(-90.44, 18.56) * mm});
            skLineSegment(sketch, "E677", {"start": v(-90.44, 18.56) * mm, "end": v(-89.99, 18.7) * mm});
            skLineSegment(sketch, "E678", {"start": v(-89.99, 18.7) * mm, "end": v(-89.6, 18.75) * mm});
            skLineSegment(sketch, "E679", {"start": v(-89.6, 18.75) * mm, "end": v(-88.86, 18.52) * mm});
            skLineSegment(sketch, "E680", {"start": v(-88.86, 18.52) * mm, "end": v(-88.59, 17.9) * mm});
            skLineSegment(sketch, "E681", {"start": v(-88.59, 17.9) * mm, "end": v(-88.65, 17.56) * mm});
            skLineSegment(sketch, "E682", {"start": v(-88.65, 17.56) * mm, "end": v(-88.9, 17.17) * mm});
            skLineSegment(sketch, "E683", {"start": v(-88.9, 17.17) * mm, "end": v(-89.22, 16.84) * mm});
            skLineSegment(sketch, "E684", {"start": v(-89.22, 16.84) * mm, "end": v(-89.97, 16.06) * mm});
            skLineSegment(sketch, "E685", {"start": v(-80.78, 17.36) * mm, "end": v(-80.33, 17.1) * mm});
            skLineSegment(sketch, "E686", {"start": v(-80.33, 17.1) * mm, "end": v(-80.16, 16.62) * mm});
            skLineSegment(sketch, "E687", {"start": v(-80.16, 16.62) * mm, "end": v(-80.47, 15.94) * mm});
            skLineSegment(sketch, "E688", {"start": v(-80.47, 15.94) * mm, "end": v(-81.33, 15.7) * mm});
            skLineSegment(sketch, "E689", {"start": v(-81.33, 15.7) * mm, "end": v(-81.71, 15.73) * mm});
            skLineSegment(sketch, "E690", {"start": v(-81.71, 15.73) * mm, "end": v(-82.12, 15.84) * mm});
            skLineSegment(sketch, "E691", {"start": v(-82.12, 15.84) * mm, "end": v(-82.12, 16.23) * mm});
            skLineSegment(sketch, "E692", {"start": v(-82.12, 16.23) * mm, "end": v(-81.76, 16.08) * mm});
            skLineSegment(sketch, "E693", {"start": v(-81.76, 16.08) * mm, "end": v(-81.34, 16.03) * mm});
            skLineSegment(sketch, "E694", {"start": v(-81.34, 16.03) * mm, "end": v(-80.76, 16.18) * mm});
            skLineSegment(sketch, "E695", {"start": v(-80.76, 16.18) * mm, "end": v(-80.57, 16.62) * mm});
            skLineSegment(sketch, "E696", {"start": v(-80.57, 16.62) * mm, "end": v(-80.75, 17.03) * mm});
            skLineSegment(sketch, "E697", {"start": v(-80.75, 17.03) * mm, "end": v(-81.26, 17.18) * mm});
            skLineSegment(sketch, "E698", {"start": v(-81.26, 17.18) * mm, "end": v(-81.6, 17.18) * mm});
            skLineSegment(sketch, "E699", {"start": v(-81.6, 17.18) * mm, "end": v(-81.6, 17.5) * mm});
            skLineSegment(sketch, "E700", {"start": v(-81.6, 17.5) * mm, "end": v(-81.25, 17.5) * mm});
            skLineSegment(sketch, "E701", {"start": v(-81.25, 17.5) * mm, "end": v(-80.8, 17.63) * mm});
            skLineSegment(sketch, "E702", {"start": v(-80.8, 17.63) * mm, "end": v(-80.63, 17.97) * mm});
            skLineSegment(sketch, "E703", {"start": v(-80.63, 17.97) * mm, "end": v(-80.8, 18.32) * mm});
            skLineSegment(sketch, "E704", {"start": v(-80.8, 18.32) * mm, "end": v(-81.26, 18.44) * mm});
            skLineSegment(sketch, "E705", {"start": v(-81.26, 18.44) * mm, "end": v(-81.62, 18.4) * mm});
            skLineSegment(sketch, "E706", {"start": v(-81.62, 18.4) * mm, "end": v(-82.03, 18.3) * mm});
            skLineSegment(sketch, "E707", {"start": v(-82.03, 18.3) * mm, "end": v(-82.03, 18.66) * mm});
            skLineSegment(sketch, "E708", {"start": v(-82.03, 18.66) * mm, "end": v(-81.6, 18.75) * mm});
            skLineSegment(sketch, "E709", {"start": v(-81.6, 18.75) * mm, "end": v(-81.23, 18.78) * mm});
            skLineSegment(sketch, "E710", {"start": v(-81.23, 18.78) * mm, "end": v(-80.5, 18.58) * mm});
            skLineSegment(sketch, "E711", {"start": v(-80.5, 18.58) * mm, "end": v(-80.23, 18.01) * mm});
            skLineSegment(sketch, "E712", {"start": v(-80.23, 18.01) * mm, "end": v(-80.37, 17.6) * mm});
            skLineSegment(sketch, "E713", {"start": v(-80.37, 17.6) * mm, "end": v(-80.78, 17.36) * mm});
            skLineSegment(sketch, "E714", {"start": v(-72.52, 18.24) * mm, "end": v(-73.53, 16.65) * mm});
            skLineSegment(sketch, "E715", {"start": v(-73.53, 16.65) * mm, "end": v(-72.52, 16.65) * mm});
            skLineSegment(sketch, "E716", {"start": v(-72.52, 16.65) * mm, "end": v(-72.52, 18.24) * mm});
            skLineSegment(sketch, "E717", {"start": v(-72.62, 18.6) * mm, "end": v(-72.11, 18.6) * mm});
            skLineSegment(sketch, "E718", {"start": v(-72.11, 18.6) * mm, "end": v(-72.11, 16.65) * mm});
            skLineSegment(sketch, "E719", {"start": v(-72.11, 16.65) * mm, "end": v(-71.69, 16.65) * mm});
            skLineSegment(sketch, "E720", {"start": v(-71.69, 16.65) * mm, "end": v(-71.69, 16.32) * mm});
            skLineSegment(sketch, "E721", {"start": v(-71.69, 16.32) * mm, "end": v(-72.11, 16.32) * mm});
            skLineSegment(sketch, "E722", {"start": v(-72.11, 16.32) * mm, "end": v(-72.11, 15.61) * mm});
            skLineSegment(sketch, "E723", {"start": v(-72.11, 15.61) * mm, "end": v(-72.52, 15.61) * mm});
            skLineSegment(sketch, "E724", {"start": v(-72.52, 15.61) * mm, "end": v(-72.52, 16.32) * mm});
            skLineSegment(sketch, "E725", {"start": v(-72.52, 16.32) * mm, "end": v(-73.86, 16.32) * mm});
            skLineSegment(sketch, "E726", {"start": v(-73.86, 16.32) * mm, "end": v(-73.86, 16.7) * mm});
            skLineSegment(sketch, "E727", {"start": v(-73.86, 16.7) * mm, "end": v(-72.62, 18.6) * mm});
            skLineSegment(sketch, "E728", {"start": v(16.47, -9.48) * mm, "end": v(16.88, -9.48) * mm});
            skLineSegment(sketch, "E729", {"start": v(16.88, -9.48) * mm, "end": v(16.88, -11.28) * mm});
            skLineSegment(sketch, "E730", {"start": v(16.88, -11.28) * mm, "end": v(17.05, -11.97) * mm});
            skLineSegment(sketch, "E731", {"start": v(17.05, -11.97) * mm, "end": v(17.61, -12.18) * mm});
            skLineSegment(sketch, "E732", {"start": v(17.61, -12.18) * mm, "end": v(18.17, -11.97) * mm});
            skLineSegment(sketch, "E733", {"start": v(18.17, -11.97) * mm, "end": v(18.35, -11.28) * mm});
            skLineSegment(sketch, "E734", {"start": v(18.35, -11.28) * mm, "end": v(18.35, -9.48) * mm});
            skLineSegment(sketch, "E735", {"start": v(18.35, -9.48) * mm, "end": v(18.75, -9.48) * mm});
            skLineSegment(sketch, "E736", {"start": v(18.75, -9.48) * mm, "end": v(18.75, -11.33) * mm});
            skLineSegment(sketch, "E737", {"start": v(18.75, -11.33) * mm, "end": v(18.46, -12.21) * mm});
            skLineSegment(sketch, "E738", {"start": v(18.46, -12.21) * mm, "end": v(17.61, -12.51) * mm});
            skLineSegment(sketch, "E739", {"start": v(17.61, -12.51) * mm, "end": v(16.76, -12.21) * mm});
            skLineSegment(sketch, "E740", {"start": v(16.76, -12.21) * mm, "end": v(16.47, -11.33) * mm});
            skLineSegment(sketch, "E741", {"start": v(16.47, -11.33) * mm, "end": v(16.47, -9.48) * mm});
            skLineSegment(sketch, "E742", {"start": v(21.3, -9.57) * mm, "end": v(21.3, -9.97) * mm});
            skLineSegment(sketch, "E743", {"start": v(21.3, -9.97) * mm, "end": v(20.86, -9.8) * mm});
            skLineSegment(sketch, "E744", {"start": v(20.86, -9.8) * mm, "end": v(20.47, -9.75) * mm});
            skLineSegment(sketch, "E745", {"start": v(20.47, -9.75) * mm, "end": v(19.96, -9.88) * mm});
            skLineSegment(sketch, "E746", {"start": v(19.96, -9.88) * mm, "end": v(19.78, -10.24) * mm});
            skLineSegment(sketch, "E747", {"start": v(19.78, -10.24) * mm, "end": v(19.9, -10.54) * mm});
            skLineSegment(sketch, "E748", {"start": v(19.9, -10.54) * mm, "end": v(20.35, -10.7) * mm});
            skLineSegment(sketch, "E749", {"start": v(20.35, -10.7) * mm, "end": v(20.6, -10.75) * mm});
            skLineSegment(sketch, "E750", {"start": v(20.6, -10.75) * mm, "end": v(21.26, -11.05) * mm});
            skLineSegment(sketch, "E751", {"start": v(21.26, -11.05) * mm, "end": v(21.47, -11.63) * mm});
            skLineSegment(sketch, "E752", {"start": v(21.47, -11.63) * mm, "end": v(21.18, -12.29) * mm});
            skLineSegment(sketch, "E753", {"start": v(21.18, -12.29) * mm, "end": v(20.33, -12.51) * mm});
            skLineSegment(sketch, "E754", {"start": v(20.33, -12.51) * mm, "end": v(19.88, -12.46) * mm});
            skLineSegment(sketch, "E755", {"start": v(19.88, -12.46) * mm, "end": v(19.39, -12.32) * mm});
            skLineSegment(sketch, "E756", {"start": v(19.39, -12.32) * mm, "end": v(19.39, -11.9) * mm});
            skLineSegment(sketch, "E757", {"start": v(19.39, -11.9) * mm, "end": v(19.87, -12.11) * mm});
            skLineSegment(sketch, "E758", {"start": v(19.87, -12.11) * mm, "end": v(20.33, -12.18) * mm});
            skLineSegment(sketch, "E759", {"start": v(20.33, -12.18) * mm, "end": v(20.86, -12.05) * mm});
            skLineSegment(sketch, "E760", {"start": v(20.86, -12.05) * mm, "end": v(21.05, -11.66) * mm});
            skLineSegment(sketch, "E761", {"start": v(21.05, -11.66) * mm, "end": v(20.92, -11.32) * mm});
            skLineSegment(sketch, "E762", {"start": v(20.92, -11.32) * mm, "end": v(20.48, -11.13) * mm});
            skLineSegment(sketch, "E763", {"start": v(20.48, -11.13) * mm, "end": v(20.23, -11.08) * mm});
            skLineSegment(sketch, "E764", {"start": v(20.23, -11.08) * mm, "end": v(19.58, -10.8) * mm});
            skLineSegment(sketch, "E765", {"start": v(19.58, -10.8) * mm, "end": v(19.38, -10.27) * mm});
            skLineSegment(sketch, "E766", {"start": v(19.38, -10.27) * mm, "end": v(19.65, -9.65) * mm});
            skLineSegment(sketch, "E767", {"start": v(19.65, -9.65) * mm, "end": v(20.42, -9.42) * mm});
            skLineSegment(sketch, "E768", {"start": v(20.42, -9.42) * mm, "end": v(20.85, -9.46) * mm});
            skLineSegment(sketch, "E769", {"start": v(20.85, -9.46) * mm, "end": v(21.3, -9.57) * mm});
            skLineSegment(sketch, "E770", {"start": v(22.5, -11.03) * mm, "end": v(22.5, -12.12) * mm});
            skLineSegment(sketch, "E771", {"start": v(22.5, -12.12) * mm, "end": v(23.15, -12.12) * mm});
            skLineSegment(sketch, "E772", {"start": v(23.15, -12.12) * mm, "end": v(23.63, -11.99) * mm});
            skLineSegment(sketch, "E773", {"start": v(23.63, -11.99) * mm, "end": v(23.79, -11.57) * mm});
            skLineSegment(sketch, "E774", {"start": v(23.79, -11.57) * mm, "end": v(23.63, -11.16) * mm});
            skLineSegment(sketch, "E775", {"start": v(23.63, -11.16) * mm, "end": v(23.15, -11.03) * mm});
            skLineSegment(sketch, "E776", {"start": v(23.15, -11.03) * mm, "end": v(22.5, -11.03) * mm});
            skLineSegment(sketch, "E777", {"start": v(22.5, -9.8) * mm, "end": v(22.5, -10.7) * mm});
            skLineSegment(sketch, "E778", {"start": v(22.5, -10.7) * mm, "end": v(23.1, -10.7) * mm});
            skLineSegment(sketch, "E779", {"start": v(23.1, -10.7) * mm, "end": v(23.54, -10.6) * mm});
            skLineSegment(sketch, "E780", {"start": v(23.54, -10.6) * mm, "end": v(23.68, -10.25) * mm});
            skLineSegment(sketch, "E781", {"start": v(23.68, -10.25) * mm, "end": v(23.54, -9.92) * mm});
            skLineSegment(sketch, "E782", {"start": v(23.54, -9.92) * mm, "end": v(23.1, -9.8) * mm});
            skLineSegment(sketch, "E783", {"start": v(23.1, -9.8) * mm, "end": v(22.5, -9.8) * mm});
            skLineSegment(sketch, "E784", {"start": v(22.1, -9.48) * mm, "end": v(23.13, -9.48) * mm});
            skLineSegment(sketch, "E785", {"start": v(23.13, -9.48) * mm, "end": v(23.84, -9.67) * mm});
            skLineSegment(sketch, "E786", {"start": v(23.84, -9.67) * mm, "end": v(24.09, -10.21) * mm});
            skLineSegment(sketch, "E787", {"start": v(24.09, -10.21) * mm, "end": v(23.96, -10.65) * mm});
            skLineSegment(sketch, "E788", {"start": v(23.96, -10.65) * mm, "end": v(23.59, -10.85) * mm});
            skLineSegment(sketch, "E789", {"start": v(23.59, -10.85) * mm, "end": v(24.05, -11.11) * mm});
            skLineSegment(sketch, "E790", {"start": v(24.05, -11.11) * mm, "end": v(24.21, -11.62) * mm});
            skLineSegment(sketch, "E791", {"start": v(24.21, -11.62) * mm, "end": v(23.94, -12.24) * mm});
            skLineSegment(sketch, "E792", {"start": v(23.94, -12.24) * mm, "end": v(23.17, -12.45) * mm});
            skLineSegment(sketch, "E793", {"start": v(23.17, -12.45) * mm, "end": v(22.1, -12.45) * mm});
            skLineSegment(sketch, "E794", {"start": v(22.1, -12.45) * mm, "end": v(22.1, -9.48) * mm});
            skLineSegment(sketch, "E795", {"start": v(17.95, -16.43) * mm, "end": v(17.33, -16.54) * mm});
            skLineSegment(sketch, "E796", {"start": v(17.33, -16.54) * mm, "end": v(17.16, -16.88) * mm});
            skLineSegment(sketch, "E797", {"start": v(17.16, -16.88) * mm, "end": v(17.3, -17.2) * mm});
            skLineSegment(sketch, "E798", {"start": v(17.3, -17.2) * mm, "end": v(17.64, -17.3) * mm});
            skLineSegment(sketch, "E799", {"start": v(17.64, -17.3) * mm, "end": v(18.13, -17.1) * mm});
            skLineSegment(sketch, "E800", {"start": v(18.13, -17.1) * mm, "end": v(18.32, -16.52) * mm});
            skLineSegment(sketch, "E801", {"start": v(18.32, -16.52) * mm, "end": v(18.32, -16.43) * mm});
            skLineSegment(sketch, "E802", {"start": v(18.32, -16.43) * mm, "end": v(17.95, -16.43) * mm});
            skLineSegment(sketch, "E803", {"start": v(18.68, -16.28) * mm, "end": v(18.68, -17.56) * mm});
            skLineSegment(sketch, "E804", {"start": v(18.68, -17.56) * mm, "end": v(18.32, -17.56) * mm});
            skLineSegment(sketch, "E805", {"start": v(18.32, -17.56) * mm, "end": v(18.32, -17.22) * mm});
            skLineSegment(sketch, "E806", {"start": v(18.32, -17.22) * mm, "end": v(18, -17.52) * mm});
            skLineSegment(sketch, "E807", {"start": v(18, -17.52) * mm, "end": v(17.55, -17.61) * mm});
            skLineSegment(sketch, "E808", {"start": v(17.55, -17.61) * mm, "end": v(17, -17.42) * mm});
            skLineSegment(sketch, "E809", {"start": v(17, -17.42) * mm, "end": v(16.8, -16.9) * mm});
            skLineSegment(sketch, "E810", {"start": v(16.8, -16.9) * mm, "end": v(17.05, -16.34) * mm});
            skLineSegment(sketch, "E811", {"start": v(17.05, -16.34) * mm, "end": v(17.8, -16.15) * mm});
            skLineSegment(sketch, "E812", {"start": v(17.8, -16.15) * mm, "end": v(18.32, -16.15) * mm});
            skLineSegment(sketch, "E813", {"start": v(18.32, -16.15) * mm, "end": v(18.32, -16.11) * mm});
            skLineSegment(sketch, "E814", {"start": v(18.32, -16.11) * mm, "end": v(18.15, -15.72) * mm});
            skLineSegment(sketch, "E815", {"start": v(18.15, -15.72) * mm, "end": v(17.68, -15.58) * mm});
            skLineSegment(sketch, "E816", {"start": v(17.68, -15.58) * mm, "end": v(17.31, -15.63) * mm});
            skLineSegment(sketch, "E817", {"start": v(17.31, -15.63) * mm, "end": v(16.96, -15.76) * mm});
            skLineSegment(sketch, "E818", {"start": v(16.96, -15.76) * mm, "end": v(16.96, -15.43) * mm});
            skLineSegment(sketch, "E819", {"start": v(16.96, -15.43) * mm, "end": v(17.35, -15.3) * mm});
            skLineSegment(sketch, "E820", {"start": v(17.35, -15.3) * mm, "end": v(17.72, -15.27) * mm});
            skLineSegment(sketch, "E821", {"start": v(17.72, -15.27) * mm, "end": v(18.44, -15.52) * mm});
            skLineSegment(sketch, "E822", {"start": v(18.44, -15.52) * mm, "end": v(18.68, -16.28) * mm});
            skLineSegment(sketch, "E823", {"start": v(19.4, -16.67) * mm, "end": v(19.4, -15.32) * mm});
            skLineSegment(sketch, "E824", {"start": v(19.4, -15.32) * mm, "end": v(19.77, -15.32) * mm});
            skLineSegment(sketch, "E825", {"start": v(19.77, -15.32) * mm, "end": v(19.77, -16.66) * mm});
            skLineSegment(sketch, "E826", {"start": v(19.77, -16.66) * mm, "end": v(19.9, -17.14) * mm});
            skLineSegment(sketch, "E827", {"start": v(19.9, -17.14) * mm, "end": v(20.26, -17.3) * mm});
            skLineSegment(sketch, "E828", {"start": v(20.26, -17.3) * mm, "end": v(20.73, -17.1) * mm});
            skLineSegment(sketch, "E829", {"start": v(20.73, -17.1) * mm, "end": v(20.9, -16.59) * mm});
            skLineSegment(sketch, "E830", {"start": v(20.9, -16.59) * mm, "end": v(20.9, -15.32) * mm});
            skLineSegment(sketch, "E831", {"start": v(20.9, -15.32) * mm, "end": v(21.27, -15.32) * mm});
            skLineSegment(sketch, "E832", {"start": v(21.27, -15.32) * mm, "end": v(21.27, -17.56) * mm});
            skLineSegment(sketch, "E833", {"start": v(21.27, -17.56) * mm, "end": v(20.9, -17.56) * mm});
            skLineSegment(sketch, "E834", {"start": v(20.9, -17.56) * mm, "end": v(20.9, -17.21) * mm});
            skLineSegment(sketch, "E835", {"start": v(20.9, -17.21) * mm, "end": v(20.6, -17.52) * mm});
            skLineSegment(sketch, "E836", {"start": v(20.6, -17.52) * mm, "end": v(20.19, -17.61) * mm});
            skLineSegment(sketch, "E837", {"start": v(20.19, -17.61) * mm, "end": v(19.6, -17.38) * mm});
            skLineSegment(sketch, "E838", {"start": v(19.6, -17.38) * mm, "end": v(19.4, -16.67) * mm});
            skLineSegment(sketch, "E839", {"start": v(23.89, -15.32) * mm, "end": v(23.08, -16.41) * mm});
            skLineSegment(sketch, "E840", {"start": v(23.08, -16.41) * mm, "end": v(23.93, -17.56) * mm});
            skLineSegment(sketch, "E841", {"start": v(23.93, -17.56) * mm, "end": v(23.5, -17.56) * mm});
            skLineSegment(sketch, "E842", {"start": v(23.5, -17.56) * mm, "end": v(22.85, -16.68) * mm});
            skLineSegment(sketch, "E843", {"start": v(22.85, -16.68) * mm, "end": v(22.2, -17.56) * mm});
            skLineSegment(sketch, "E844", {"start": v(22.2, -17.56) * mm, "end": v(21.77, -17.56) * mm});
            skLineSegment(sketch, "E845", {"start": v(21.77, -17.56) * mm, "end": v(22.63, -16.39) * mm});
            skLineSegment(sketch, "E846", {"start": v(22.63, -16.39) * mm, "end": v(21.84, -15.32) * mm});
            skLineSegment(sketch, "E847", {"start": v(21.84, -15.32) * mm, "end": v(22.27, -15.32) * mm});
            skLineSegment(sketch, "E848", {"start": v(22.27, -15.32) * mm, "end": v(22.86, -16.12) * mm});
            skLineSegment(sketch, "E849", {"start": v(22.86, -16.12) * mm, "end": v(23.46, -15.32) * mm});
            skLineSegment(sketch, "E850", {"start": v(23.46, -15.32) * mm, "end": v(23.89, -15.32) * mm});
            skLineSegment(sketch, "E851", {"start": v(28.33, -9.48) * mm, "end": v(28.74, -9.48) * mm});
            skLineSegment(sketch, "E852", {"start": v(28.74, -9.48) * mm, "end": v(28.74, -11.28) * mm});
            skLineSegment(sketch, "E853", {"start": v(28.74, -11.28) * mm, "end": v(28.91, -11.97) * mm});
            skLineSegment(sketch, "E854", {"start": v(28.91, -11.97) * mm, "end": v(29.47, -12.18) * mm});
            skLineSegment(sketch, "E855", {"start": v(29.47, -12.18) * mm, "end": v(30.03, -11.97) * mm});
            skLineSegment(sketch, "E856", {"start": v(30.03, -11.97) * mm, "end": v(30.2, -11.28) * mm});
            skLineSegment(sketch, "E857", {"start": v(30.2, -11.28) * mm, "end": v(30.2, -9.48) * mm});
            skLineSegment(sketch, "E858", {"start": v(30.2, -9.48) * mm, "end": v(30.61, -9.48) * mm});
            skLineSegment(sketch, "E859", {"start": v(30.61, -9.48) * mm, "end": v(30.61, -11.33) * mm});
            skLineSegment(sketch, "E860", {"start": v(30.61, -11.33) * mm, "end": v(30.32, -12.21) * mm});
            skLineSegment(sketch, "E861", {"start": v(30.32, -12.21) * mm, "end": v(29.47, -12.51) * mm});
            skLineSegment(sketch, "E862", {"start": v(29.47, -12.51) * mm, "end": v(28.62, -12.21) * mm});
            skLineSegment(sketch, "E863", {"start": v(28.62, -12.21) * mm, "end": v(28.33, -11.33) * mm});
            skLineSegment(sketch, "E864", {"start": v(28.33, -11.33) * mm, "end": v(28.33, -9.48) * mm});
            skLineSegment(sketch, "E865", {"start": v(33.15, -9.57) * mm, "end": v(33.15, -9.97) * mm});
            skLineSegment(sketch, "E866", {"start": v(33.15, -9.97) * mm, "end": v(32.72, -9.8) * mm});
            skLineSegment(sketch, "E867", {"start": v(32.72, -9.8) * mm, "end": v(32.33, -9.75) * mm});
            skLineSegment(sketch, "E868", {"start": v(32.33, -9.75) * mm, "end": v(31.82, -9.88) * mm});
            skLineSegment(sketch, "E869", {"start": v(31.82, -9.88) * mm, "end": v(31.64, -10.24) * mm});
            skLineSegment(sketch, "E870", {"start": v(31.64, -10.24) * mm, "end": v(31.76, -10.54) * mm});
            skLineSegment(sketch, "E871", {"start": v(31.76, -10.54) * mm, "end": v(32.21, -10.7) * mm});
            skLineSegment(sketch, "E872", {"start": v(32.21, -10.7) * mm, "end": v(32.45, -10.75) * mm});
            skLineSegment(sketch, "E873", {"start": v(32.45, -10.75) * mm, "end": v(33.12, -11.05) * mm});
            skLineSegment(sketch, "E874", {"start": v(33.12, -11.05) * mm, "end": v(33.33, -11.63) * mm});
            skLineSegment(sketch, "E875", {"start": v(33.33, -11.63) * mm, "end": v(33.04, -12.29) * mm});
            skLineSegment(sketch, "E876", {"start": v(33.04, -12.29) * mm, "end": v(32.2, -12.51) * mm});
            skLineSegment(sketch, "E877", {"start": v(32.2, -12.51) * mm, "end": v(31.74, -12.46) * mm});
            skLineSegment(sketch, "E878", {"start": v(31.74, -12.46) * mm, "end": v(31.25, -12.32) * mm});
            skLineSegment(sketch, "E879", {"start": v(31.25, -12.32) * mm, "end": v(31.25, -11.9) * mm});
            skLineSegment(sketch, "E880", {"start": v(31.25, -11.9) * mm, "end": v(31.73, -12.11) * mm});
            skLineSegment(sketch, "E881", {"start": v(31.73, -12.11) * mm, "end": v(32.2, -12.18) * mm});
            skLineSegment(sketch, "E882", {"start": v(32.2, -12.18) * mm, "end": v(32.73, -12.05) * mm});
            skLineSegment(sketch, "E883", {"start": v(32.73, -12.05) * mm, "end": v(32.91, -11.66) * mm});
            skLineSegment(sketch, "E884", {"start": v(32.91, -11.66) * mm, "end": v(32.78, -11.32) * mm});
            skLineSegment(sketch, "E885", {"start": v(32.78, -11.32) * mm, "end": v(32.34, -11.13) * mm});
            skLineSegment(sketch, "E886", {"start": v(32.34, -11.13) * mm, "end": v(32.1, -11.08) * mm});
            skLineSegment(sketch, "E887", {"start": v(32.1, -11.08) * mm, "end": v(31.44, -10.8) * mm});
            skLineSegment(sketch, "E888", {"start": v(31.44, -10.8) * mm, "end": v(31.24, -10.27) * mm});
            skLineSegment(sketch, "E889", {"start": v(31.24, -10.27) * mm, "end": v(31.52, -9.65) * mm});
            skLineSegment(sketch, "E890", {"start": v(31.52, -9.65) * mm, "end": v(32.28, -9.42) * mm});
            skLineSegment(sketch, "E891", {"start": v(32.28, -9.42) * mm, "end": v(32.71, -9.46) * mm});
            skLineSegment(sketch, "E892", {"start": v(32.71, -9.46) * mm, "end": v(33.15, -9.57) * mm});
            skLineSegment(sketch, "E893", {"start": v(34.36, -11.03) * mm, "end": v(34.36, -12.12) * mm});
            skLineSegment(sketch, "E894", {"start": v(34.36, -12.12) * mm, "end": v(35.01, -12.12) * mm});
            skLineSegment(sketch, "E895", {"start": v(35.01, -12.12) * mm, "end": v(35.5, -11.99) * mm});
            skLineSegment(sketch, "E896", {"start": v(35.5, -11.99) * mm, "end": v(35.65, -11.57) * mm});
            skLineSegment(sketch, "E897", {"start": v(35.65, -11.57) * mm, "end": v(35.5, -11.16) * mm});
            skLineSegment(sketch, "E898", {"start": v(35.5, -11.16) * mm, "end": v(35.01, -11.03) * mm});
            skLineSegment(sketch, "E899", {"start": v(35.01, -11.03) * mm, "end": v(34.36, -11.03) * mm});
            skLineSegment(sketch, "E900", {"start": v(34.36, -9.8) * mm, "end": v(34.36, -10.7) * mm});
            skLineSegment(sketch, "E901", {"start": v(34.36, -10.7) * mm, "end": v(34.96, -10.7) * mm});
            skLineSegment(sketch, "E902", {"start": v(34.96, -10.7) * mm, "end": v(35.4, -10.6) * mm});
            skLineSegment(sketch, "E903", {"start": v(35.4, -10.6) * mm, "end": v(35.55, -10.25) * mm});
            skLineSegment(sketch, "E904", {"start": v(35.55, -10.25) * mm, "end": v(35.4, -9.92) * mm});
            skLineSegment(sketch, "E905", {"start": v(35.4, -9.92) * mm, "end": v(34.96, -9.8) * mm});
            skLineSegment(sketch, "E906", {"start": v(34.96, -9.8) * mm, "end": v(34.36, -9.8) * mm});
            skLineSegment(sketch, "E907", {"start": v(33.96, -9.48) * mm, "end": v(35, -9.48) * mm});
            skLineSegment(sketch, "E908", {"start": v(35, -9.48) * mm, "end": v(35.7, -9.67) * mm});
            skLineSegment(sketch, "E909", {"start": v(35.7, -9.67) * mm, "end": v(35.95, -10.21) * mm});
            skLineSegment(sketch, "E910", {"start": v(35.95, -10.21) * mm, "end": v(35.82, -10.65) * mm});
            skLineSegment(sketch, "E911", {"start": v(35.82, -10.65) * mm, "end": v(35.45, -10.85) * mm});
            skLineSegment(sketch, "E912", {"start": v(35.45, -10.85) * mm, "end": v(35.9, -11.11) * mm});
            skLineSegment(sketch, "E913", {"start": v(35.9, -11.11) * mm, "end": v(36.07, -11.62) * mm});
            skLineSegment(sketch, "E914", {"start": v(36.07, -11.62) * mm, "end": v(35.8, -12.24) * mm});
            skLineSegment(sketch, "E915", {"start": v(35.8, -12.24) * mm, "end": v(35.03, -12.45) * mm});
            skLineSegment(sketch, "E916", {"start": v(35.03, -12.45) * mm, "end": v(33.96, -12.45) * mm});
            skLineSegment(sketch, "E917", {"start": v(33.96, -12.45) * mm, "end": v(33.96, -9.48) * mm});
            skLineSegment(sketch, "E918", {"start": v(30, -16.2) * mm, "end": v(30, -17.56) * mm});
            skLineSegment(sketch, "E919", {"start": v(30, -17.56) * mm, "end": v(29.63, -17.56) * mm});
            skLineSegment(sketch, "E920", {"start": v(29.63, -17.56) * mm, "end": v(29.63, -16.22) * mm});
            skLineSegment(sketch, "E921", {"start": v(29.63, -16.22) * mm, "end": v(29.5, -15.75) * mm});
            skLineSegment(sketch, "E922", {"start": v(29.5, -15.75) * mm, "end": v(29.14, -15.59) * mm});
            skLineSegment(sketch, "E923", {"start": v(29.14, -15.59) * mm, "end": v(28.67, -15.78) * mm});
            skLineSegment(sketch, "E924", {"start": v(28.67, -15.78) * mm, "end": v(28.5, -16.3) * mm});
            skLineSegment(sketch, "E925", {"start": v(28.5, -16.3) * mm, "end": v(28.5, -17.56) * mm});
            skLineSegment(sketch, "E926", {"start": v(28.5, -17.56) * mm, "end": v(28.13, -17.56) * mm});
            skLineSegment(sketch, "E927", {"start": v(28.13, -17.56) * mm, "end": v(28.13, -14.45) * mm});
            skLineSegment(sketch, "E928", {"start": v(28.13, -14.45) * mm, "end": v(28.5, -14.45) * mm});
            skLineSegment(sketch, "E929", {"start": v(28.5, -14.45) * mm, "end": v(28.5, -15.67) * mm});
            skLineSegment(sketch, "E930", {"start": v(28.5, -15.67) * mm, "end": v(28.8, -15.37) * mm});
            skLineSegment(sketch, "E931", {"start": v(28.8, -15.37) * mm, "end": v(29.22, -15.27) * mm});
            skLineSegment(sketch, "E932", {"start": v(29.22, -15.27) * mm, "end": v(29.8, -15.5) * mm});
            skLineSegment(sketch, "E933", {"start": v(29.8, -15.5) * mm, "end": v(30, -16.2) * mm});
            skLineSegment(sketch, "E934", {"start": v(31.6, -15.58) * mm, "end": v(31.14, -15.81) * mm});
            skLineSegment(sketch, "E935", {"start": v(31.14, -15.81) * mm, "end": v(30.96, -16.44) * mm});
            skLineSegment(sketch, "E936", {"start": v(30.96, -16.44) * mm, "end": v(31.13, -17.07) * mm});
            skLineSegment(sketch, "E937", {"start": v(31.13, -17.07) * mm, "end": v(31.6, -17.3) * mm});
            skLineSegment(sketch, "E938", {"start": v(31.6, -17.3) * mm, "end": v(32.07, -17.07) * mm});
            skLineSegment(sketch, "E939", {"start": v(32.07, -17.07) * mm, "end": v(32.24, -16.44) * mm});
            skLineSegment(sketch, "E940", {"start": v(32.24, -16.44) * mm, "end": v(32.07, -15.81) * mm});
            skLineSegment(sketch, "E941", {"start": v(32.07, -15.81) * mm, "end": v(31.6, -15.58) * mm});
            skLineSegment(sketch, "E942", {"start": v(31.6, -15.27) * mm, "end": v(32.35, -15.58) * mm});
            skLineSegment(sketch, "E943", {"start": v(32.35, -15.58) * mm, "end": v(32.63, -16.44) * mm});
            skLineSegment(sketch, "E944", {"start": v(32.63, -16.44) * mm, "end": v(32.35, -17.3) * mm});
            skLineSegment(sketch, "E945", {"start": v(32.35, -17.3) * mm, "end": v(31.6, -17.61) * mm});
            skLineSegment(sketch, "E946", {"start": v(31.6, -17.61) * mm, "end": v(30.85, -17.3) * mm});
            skLineSegment(sketch, "E947", {"start": v(30.85, -17.3) * mm, "end": v(30.58, -16.44) * mm});
            skLineSegment(sketch, "E948", {"start": v(30.58, -16.44) * mm, "end": v(30.85, -15.58) * mm});
            skLineSegment(sketch, "E949", {"start": v(30.85, -15.58) * mm, "end": v(31.6, -15.27) * mm});
            skLineSegment(sketch, "E950", {"start": v(34.66, -15.39) * mm, "end": v(34.66, -15.74) * mm});
            skLineSegment(sketch, "E951", {"start": v(34.66, -15.74) * mm, "end": v(34.33, -15.62) * mm});
            skLineSegment(sketch, "E952", {"start": v(34.33, -15.62) * mm, "end": v(33.99, -15.58) * mm});
            skLineSegment(sketch, "E953", {"start": v(33.99, -15.58) * mm, "end": v(33.58, -15.66) * mm});
            skLineSegment(sketch, "E954", {"start": v(33.58, -15.66) * mm, "end": v(33.44, -15.91) * mm});
            skLineSegment(sketch, "E955", {"start": v(33.44, -15.91) * mm, "end": v(33.54, -16.11) * mm});
            skLineSegment(sketch, "E956", {"start": v(33.54, -16.11) * mm, "end": v(33.93, -16.25) * mm});
            skLineSegment(sketch, "E957", {"start": v(33.93, -16.25) * mm, "end": v(34.06, -16.28) * mm});
            skLineSegment(sketch, "E958", {"start": v(34.06, -16.28) * mm, "end": v(34.6, -16.52) * mm});
            skLineSegment(sketch, "E959", {"start": v(34.6, -16.52) * mm, "end": v(34.78, -16.94) * mm});
            skLineSegment(sketch, "E960", {"start": v(34.78, -16.94) * mm, "end": v(34.53, -17.43) * mm});
            skLineSegment(sketch, "E961", {"start": v(34.53, -17.43) * mm, "end": v(33.85, -17.61) * mm});
            skLineSegment(sketch, "E962", {"start": v(33.85, -17.61) * mm, "end": v(33.48, -17.58) * mm});
            skLineSegment(sketch, "E963", {"start": v(33.48, -17.58) * mm, "end": v(33.07, -17.48) * mm});
            skLineSegment(sketch, "E964", {"start": v(33.07, -17.48) * mm, "end": v(33.07, -17.1) * mm});
            skLineSegment(sketch, "E965", {"start": v(33.07, -17.1) * mm, "end": v(33.47, -17.26) * mm});
            skLineSegment(sketch, "E966", {"start": v(33.47, -17.26) * mm, "end": v(33.86, -17.3) * mm});
            skLineSegment(sketch, "E967", {"start": v(33.86, -17.3) * mm, "end": v(34.26, -17.22) * mm});
            skLineSegment(sketch, "E968", {"start": v(34.26, -17.22) * mm, "end": v(34.4, -16.97) * mm});
            skLineSegment(sketch, "E969", {"start": v(34.4, -16.97) * mm, "end": v(34.3, -16.74) * mm});
            skLineSegment(sketch, "E970", {"start": v(34.3, -16.74) * mm, "end": v(33.86, -16.59) * mm});
            skLineSegment(sketch, "E971", {"start": v(33.86, -16.59) * mm, "end": v(33.73, -16.56) * mm});
            skLineSegment(sketch, "E972", {"start": v(33.73, -16.56) * mm, "end": v(33.24, -16.34) * mm});
            skLineSegment(sketch, "E973", {"start": v(33.24, -16.34) * mm, "end": v(33.09, -15.93) * mm});
            skLineSegment(sketch, "E974", {"start": v(33.09, -15.93) * mm, "end": v(33.3, -15.44) * mm});
            skLineSegment(sketch, "E975", {"start": v(33.3, -15.44) * mm, "end": v(33.94, -15.27) * mm});
            skLineSegment(sketch, "E976", {"start": v(33.94, -15.27) * mm, "end": v(34.33, -15.3) * mm});
            skLineSegment(sketch, "E977", {"start": v(34.33, -15.3) * mm, "end": v(34.66, -15.39) * mm});
            skLineSegment(sketch, "E978", {"start": v(35.72, -14.69) * mm, "end": v(35.72, -15.32) * mm});
            skLineSegment(sketch, "E979", {"start": v(35.72, -15.32) * mm, "end": v(36.48, -15.32) * mm});
            skLineSegment(sketch, "E980", {"start": v(36.48, -15.32) * mm, "end": v(36.48, -15.6) * mm});
            skLineSegment(sketch, "E981", {"start": v(36.48, -15.6) * mm, "end": v(35.72, -15.6) * mm});
            skLineSegment(sketch, "E982", {"start": v(35.72, -15.6) * mm, "end": v(35.72, -16.82) * mm});
            skLineSegment(sketch, "E983", {"start": v(35.72, -16.82) * mm, "end": v(35.8, -17.17) * mm});
            skLineSegment(sketch, "E984", {"start": v(35.8, -17.17) * mm, "end": v(36.1, -17.25) * mm});
            skLineSegment(sketch, "E985", {"start": v(36.1, -17.25) * mm, "end": v(36.48, -17.25) * mm});
            skLineSegment(sketch, "E986", {"start": v(36.48, -17.25) * mm, "end": v(36.48, -17.56) * mm});
            skLineSegment(sketch, "E987", {"start": v(36.48, -17.56) * mm, "end": v(36.1, -17.56) * mm});
            skLineSegment(sketch, "E988", {"start": v(36.1, -17.56) * mm, "end": v(35.52, -17.4) * mm});
            skLineSegment(sketch, "E989", {"start": v(35.52, -17.4) * mm, "end": v(35.36, -16.82) * mm});
            skLineSegment(sketch, "E990", {"start": v(35.36, -16.82) * mm, "end": v(35.36, -15.6) * mm});
            skLineSegment(sketch, "E991", {"start": v(35.36, -15.6) * mm, "end": v(35.09, -15.6) * mm});
            skLineSegment(sketch, "E992", {"start": v(35.09, -15.6) * mm, "end": v(35.09, -15.32) * mm});
            skLineSegment(sketch, "E993", {"start": v(35.09, -15.32) * mm, "end": v(35.36, -15.32) * mm});
            skLineSegment(sketch, "E994", {"start": v(35.36, -15.32) * mm, "end": v(35.36, -14.69) * mm});
            skLineSegment(sketch, "E995", {"start": v(35.36, -14.69) * mm, "end": v(35.72, -14.69) * mm});
            skLineSegment(sketch, "E996", {"start": v(39.63, -14.91) * mm, "end": v(39.63, -16.03) * mm});
            skLineSegment(sketch, "E997", {"start": v(39.63, -16.03) * mm, "end": v(40.14, -16.03) * mm});
            skLineSegment(sketch, "E998", {"start": v(40.14, -16.03) * mm, "end": v(40.57, -15.88) * mm});
            skLineSegment(sketch, "E999", {"start": v(40.57, -15.88) * mm, "end": v(40.72, -15.47) * mm});
            skLineSegment(sketch, "E1000", {"start": v(40.72, -15.47) * mm, "end": v(40.57, -15.06) * mm});
            skLineSegment(sketch, "E1001", {"start": v(40.57, -15.06) * mm, "end": v(40.14, -14.91) * mm});
            skLineSegment(sketch, "E1002", {"start": v(40.14, -14.91) * mm, "end": v(39.63, -14.91) * mm});
            skLineSegment(sketch, "E1003", {"start": v(39.23, -14.58) * mm, "end": v(40.14, -14.58) * mm});
            skLineSegment(sketch, "E1004", {"start": v(40.14, -14.58) * mm, "end": v(40.9, -14.8) * mm});
            skLineSegment(sketch, "E1005", {"start": v(40.9, -14.8) * mm, "end": v(41.15, -15.47) * mm});
            skLineSegment(sketch, "E1006", {"start": v(41.15, -15.47) * mm, "end": v(40.9, -16.14) * mm});
            skLineSegment(sketch, "E1007", {"start": v(40.9, -16.14) * mm, "end": v(40.14, -16.36) * mm});
            skLineSegment(sketch, "E1008", {"start": v(40.14, -16.36) * mm, "end": v(39.63, -16.36) * mm});
            skLineSegment(sketch, "E1009", {"start": v(39.63, -16.36) * mm, "end": v(39.63, -17.56) * mm});
            skLineSegment(sketch, "E1010", {"start": v(39.63, -17.56) * mm, "end": v(39.23, -17.56) * mm});
            skLineSegment(sketch, "E1011", {"start": v(39.23, -17.56) * mm, "end": v(39.23, -14.58) * mm});
            skLineSegment(sketch, "E1012", {"start": v(42.4, -15.58) * mm, "end": v(41.93, -15.81) * mm});
            skLineSegment(sketch, "E1013", {"start": v(41.93, -15.81) * mm, "end": v(41.76, -16.44) * mm});
            skLineSegment(sketch, "E1014", {"start": v(41.76, -16.44) * mm, "end": v(41.93, -17.07) * mm});
            skLineSegment(sketch, "E1015", {"start": v(41.93, -17.07) * mm, "end": v(42.4, -17.3) * mm});
            skLineSegment(sketch, "E1016", {"start": v(42.4, -17.3) * mm, "end": v(42.86, -17.07) * mm});
            skLineSegment(sketch, "E1017", {"start": v(42.86, -17.07) * mm, "end": v(43.03, -16.44) * mm});
            skLineSegment(sketch, "E1018", {"start": v(43.03, -16.44) * mm, "end": v(42.86, -15.81) * mm});
            skLineSegment(sketch, "E1019", {"start": v(42.86, -15.81) * mm, "end": v(42.4, -15.58) * mm});
            skLineSegment(sketch, "E1020", {"start": v(42.4, -15.27) * mm, "end": v(43.15, -15.58) * mm});
            skLineSegment(sketch, "E1021", {"start": v(43.15, -15.58) * mm, "end": v(43.42, -16.44) * mm});
            skLineSegment(sketch, "E1022", {"start": v(43.42, -16.44) * mm, "end": v(43.15, -17.3) * mm});
            skLineSegment(sketch, "E1023", {"start": v(43.15, -17.3) * mm, "end": v(42.4, -17.61) * mm});
            skLineSegment(sketch, "E1024", {"start": v(42.4, -17.61) * mm, "end": v(41.64, -17.3) * mm});
            skLineSegment(sketch, "E1025", {"start": v(41.64, -17.3) * mm, "end": v(41.37, -16.44) * mm});
            skLineSegment(sketch, "E1026", {"start": v(41.37, -16.44) * mm, "end": v(41.64, -15.58) * mm});
            skLineSegment(sketch, "E1027", {"start": v(41.64, -15.58) * mm, "end": v(42.4, -15.27) * mm});
            skLineSegment(sketch, "E1028", {"start": v(43.81, -15.32) * mm, "end": v(44.18, -15.32) * mm});
            skLineSegment(sketch, "E1029", {"start": v(44.18, -15.32) * mm, "end": v(44.64, -17.07) * mm});
            skLineSegment(sketch, "E1030", {"start": v(44.64, -17.07) * mm, "end": v(45.1, -15.32) * mm});
            skLineSegment(sketch, "E1031", {"start": v(45.1, -15.32) * mm, "end": v(45.53, -15.32) * mm});
            skLineSegment(sketch, "E1032", {"start": v(45.53, -15.32) * mm, "end": v(45.99, -17.07) * mm});
            skLineSegment(sketch, "E1033", {"start": v(45.99, -17.07) * mm, "end": v(46.44, -15.32) * mm});
            skLineSegment(sketch, "E1034", {"start": v(46.44, -15.32) * mm, "end": v(46.81, -15.32) * mm});
            skLineSegment(sketch, "E1035", {"start": v(46.81, -15.32) * mm, "end": v(46.23, -17.56) * mm});
            skLineSegment(sketch, "E1036", {"start": v(46.23, -17.56) * mm, "end": v(45.8, -17.56) * mm});
            skLineSegment(sketch, "E1037", {"start": v(45.8, -17.56) * mm, "end": v(45.31, -15.73) * mm});
            skLineSegment(sketch, "E1038", {"start": v(45.31, -15.73) * mm, "end": v(44.83, -17.56) * mm});
            skLineSegment(sketch, "E1039", {"start": v(44.83, -17.56) * mm, "end": v(44.4, -17.56) * mm});
            skLineSegment(sketch, "E1040", {"start": v(44.4, -17.56) * mm, "end": v(43.81, -15.32) * mm});
            skLineSegment(sketch, "E1041", {"start": v(49.28, -16.35) * mm, "end": v(49.28, -16.53) * mm});
            skLineSegment(sketch, "E1042", {"start": v(49.28, -16.53) * mm, "end": v(47.6, -16.53) * mm});
            skLineSegment(sketch, "E1043", {"start": v(47.6, -16.53) * mm, "end": v(47.82, -17.1) * mm});
            skLineSegment(sketch, "E1044", {"start": v(47.82, -17.1) * mm, "end": v(48.39, -17.3) * mm});
            skLineSegment(sketch, "E1045", {"start": v(48.39, -17.3) * mm, "end": v(48.8, -17.25) * mm});
            skLineSegment(sketch, "E1046", {"start": v(48.8, -17.25) * mm, "end": v(49.2, -17.1) * mm});
            skLineSegment(sketch, "E1047", {"start": v(49.2, -17.1) * mm, "end": v(49.2, -17.44) * mm});
            skLineSegment(sketch, "E1048", {"start": v(49.2, -17.44) * mm, "end": v(48.79, -17.57) * mm});
            skLineSegment(sketch, "E1049", {"start": v(48.79, -17.57) * mm, "end": v(48.37, -17.61) * mm});
            skLineSegment(sketch, "E1050", {"start": v(48.37, -17.61) * mm, "end": v(47.52, -17.3) * mm});
            skLineSegment(sketch, "E1051", {"start": v(47.52, -17.3) * mm, "end": v(47.2, -16.46) * mm});
            skLineSegment(sketch, "E1052", {"start": v(47.2, -16.46) * mm, "end": v(47.5, -15.6) * mm});
            skLineSegment(sketch, "E1053", {"start": v(47.5, -15.6) * mm, "end": v(48.3, -15.27) * mm});
            skLineSegment(sketch, "E1054", {"start": v(48.3, -15.27) * mm, "end": v(49.02, -15.56) * mm});
            skLineSegment(sketch, "E1055", {"start": v(49.02, -15.56) * mm, "end": v(49.28, -16.35) * mm});
            skLineSegment(sketch, "E1056", {"start": v(48.91, -16.24) * mm, "end": v(48.74, -15.76) * mm});
            skLineSegment(sketch, "E1057", {"start": v(48.74, -15.76) * mm, "end": v(48.3, -15.58) * mm});
            skLineSegment(sketch, "E1058", {"start": v(48.3, -15.58) * mm, "end": v(47.82, -15.75) * mm});
            skLineSegment(sketch, "E1059", {"start": v(47.82, -15.75) * mm, "end": v(47.6, -16.24) * mm});
            skLineSegment(sketch, "E1060", {"start": v(47.6, -16.24) * mm, "end": v(48.91, -16.24) * mm});
            skLineSegment(sketch, "E1061", {"start": v(51.18, -15.67) * mm, "end": v(51.04, -15.61) * mm});
            skLineSegment(sketch, "E1062", {"start": v(51.04, -15.61) * mm, "end": v(50.88, -15.6) * mm});
            skLineSegment(sketch, "E1063", {"start": v(50.88, -15.6) * mm, "end": v(50.4, -15.8) * mm});
            skLineSegment(sketch, "E1064", {"start": v(50.4, -15.8) * mm, "end": v(50.24, -16.38) * mm});
            skLineSegment(sketch, "E1065", {"start": v(50.24, -16.38) * mm, "end": v(50.24, -17.56) * mm});
            skLineSegment(sketch, "E1066", {"start": v(50.24, -17.56) * mm, "end": v(49.87, -17.56) * mm});
            skLineSegment(sketch, "E1067", {"start": v(49.87, -17.56) * mm, "end": v(49.87, -15.32) * mm});
            skLineSegment(sketch, "E1068", {"start": v(49.87, -15.32) * mm, "end": v(50.24, -15.32) * mm});
            skLineSegment(sketch, "E1069", {"start": v(50.24, -15.32) * mm, "end": v(50.24, -15.67) * mm});
            skLineSegment(sketch, "E1070", {"start": v(50.24, -15.67) * mm, "end": v(50.54, -15.37) * mm});
            skLineSegment(sketch, "E1071", {"start": v(50.54, -15.37) * mm, "end": v(50.99, -15.27) * mm});
            skLineSegment(sketch, "E1072", {"start": v(50.99, -15.27) * mm, "end": v(51.07, -15.28) * mm});
            skLineSegment(sketch, "E1073", {"start": v(51.07, -15.28) * mm, "end": v(51.17, -15.29) * mm});
            skLineSegment(sketch, "E1074", {"start": v(51.17, -15.29) * mm, "end": v(51.18, -15.67) * mm});
            skLineSegment(sketch, "E1075", {"start": v(-34.32, -14.9) * mm, "end": v(-32.6, -14.9) * mm});
            skLineSegment(sketch, "E1076", {"start": v(-32.6, -14.9) * mm, "end": v(-32.6, -15.24) * mm});
            skLineSegment(sketch, "E1077", {"start": v(-32.6, -15.24) * mm, "end": v(-33.92, -15.24) * mm});
            skLineSegment(sketch, "E1078", {"start": v(-33.92, -15.24) * mm, "end": v(-33.92, -16.11) * mm});
            skLineSegment(sketch, "E1079", {"start": v(-33.92, -16.11) * mm, "end": v(-32.74, -16.11) * mm});
            skLineSegment(sketch, "E1080", {"start": v(-32.74, -16.11) * mm, "end": v(-32.74, -16.45) * mm});
            skLineSegment(sketch, "E1081", {"start": v(-32.74, -16.45) * mm, "end": v(-33.92, -16.45) * mm});
            skLineSegment(sketch, "E1082", {"start": v(-33.92, -16.45) * mm, "end": v(-33.92, -17.87) * mm});
            skLineSegment(sketch, "E1083", {"start": v(-33.92, -17.87) * mm, "end": v(-34.32, -17.87) * mm});
            skLineSegment(sketch, "E1084", {"start": v(-34.32, -17.87) * mm, "end": v(-34.32, -14.9) * mm});
            skLineSegment(sketch, "E1085", {"start": v(-31.98, -14.77) * mm, "end": v(-31.62, -14.77) * mm});
            skLineSegment(sketch, "E1086", {"start": v(-31.62, -14.77) * mm, "end": v(-31.62, -17.87) * mm});
            skLineSegment(sketch, "E1087", {"start": v(-31.62, -17.87) * mm, "end": v(-31.98, -17.87) * mm});
            skLineSegment(sketch, "E1088", {"start": v(-31.98, -17.87) * mm, "end": v(-31.98, -14.77) * mm});
            skLineSegment(sketch, "E1089", {"start": v(-29.84, -16.75) * mm, "end": v(-30.45, -16.85) * mm});
            skLineSegment(sketch, "E1090", {"start": v(-30.45, -16.85) * mm, "end": v(-30.62, -17.2) * mm});
            skLineSegment(sketch, "E1091", {"start": v(-30.62, -17.2) * mm, "end": v(-30.5, -17.51) * mm});
            skLineSegment(sketch, "E1092", {"start": v(-30.5, -17.51) * mm, "end": v(-30.15, -17.62) * mm});
            skLineSegment(sketch, "E1093", {"start": v(-30.15, -17.62) * mm, "end": v(-29.66, -17.4) * mm});
            skLineSegment(sketch, "E1094", {"start": v(-29.66, -17.4) * mm, "end": v(-29.47, -16.83) * mm});
            skLineSegment(sketch, "E1095", {"start": v(-29.47, -16.83) * mm, "end": v(-29.47, -16.75) * mm});
            skLineSegment(sketch, "E1096", {"start": v(-29.47, -16.75) * mm, "end": v(-29.84, -16.75) * mm});
            skLineSegment(sketch, "E1097", {"start": v(-29.1, -16.6) * mm, "end": v(-29.1, -17.87) * mm});
            skLineSegment(sketch, "E1098", {"start": v(-29.1, -17.87) * mm, "end": v(-29.47, -17.87) * mm});
            skLineSegment(sketch, "E1099", {"start": v(-29.47, -17.87) * mm, "end": v(-29.47, -17.53) * mm});
            skLineSegment(sketch, "E1100", {"start": v(-29.47, -17.53) * mm, "end": v(-29.79, -17.84) * mm});
            skLineSegment(sketch, "E1101", {"start": v(-29.79, -17.84) * mm, "end": v(-30.24, -17.93) * mm});
            skLineSegment(sketch, "E1102", {"start": v(-30.24, -17.93) * mm, "end": v(-30.8, -17.74) * mm});
            skLineSegment(sketch, "E1103", {"start": v(-30.8, -17.74) * mm, "end": v(-31, -17.22) * mm});
            skLineSegment(sketch, "E1104", {"start": v(-31, -17.22) * mm, "end": v(-30.74, -16.66) * mm});
            skLineSegment(sketch, "E1105", {"start": v(-30.74, -16.66) * mm, "end": v(-29.99, -16.46) * mm});
            skLineSegment(sketch, "E1106", {"start": v(-29.99, -16.46) * mm, "end": v(-29.47, -16.46) * mm});
            skLineSegment(sketch, "E1107", {"start": v(-29.47, -16.46) * mm, "end": v(-29.47, -16.43) * mm});
            skLineSegment(sketch, "E1108", {"start": v(-29.47, -16.43) * mm, "end": v(-29.64, -16.04) * mm});
            skLineSegment(sketch, "E1109", {"start": v(-29.64, -16.04) * mm, "end": v(-30.1, -15.9) * mm});
            skLineSegment(sketch, "E1110", {"start": v(-30.1, -15.9) * mm, "end": v(-30.48, -15.94) * mm});
            skLineSegment(sketch, "E1111", {"start": v(-30.48, -15.94) * mm, "end": v(-30.83, -16.08) * mm});
            skLineSegment(sketch, "E1112", {"start": v(-30.83, -16.08) * mm, "end": v(-30.83, -15.74) * mm});
            skLineSegment(sketch, "E1113", {"start": v(-30.83, -15.74) * mm, "end": v(-30.44, -15.63) * mm});
            skLineSegment(sketch, "E1114", {"start": v(-30.44, -15.63) * mm, "end": v(-30.07, -15.59) * mm});
            skLineSegment(sketch, "E1115", {"start": v(-30.07, -15.59) * mm, "end": v(-29.34, -15.84) * mm});
            skLineSegment(sketch, "E1116", {"start": v(-29.34, -15.84) * mm, "end": v(-29.1, -16.6) * mm});
            skLineSegment(sketch, "E1117", {"start": v(-26.92, -15.7) * mm, "end": v(-26.92, -16.05) * mm});
            skLineSegment(sketch, "E1118", {"start": v(-26.92, -16.05) * mm, "end": v(-27.25, -15.93) * mm});
            skLineSegment(sketch, "E1119", {"start": v(-27.25, -15.93) * mm, "end": v(-27.6, -15.9) * mm});
            skLineSegment(sketch, "E1120", {"start": v(-27.6, -15.9) * mm, "end": v(-28, -15.98) * mm});
            skLineSegment(sketch, "E1121", {"start": v(-28, -15.98) * mm, "end": v(-28.14, -16.23) * mm});
            skLineSegment(sketch, "E1122", {"start": v(-28.14, -16.23) * mm, "end": v(-28.04, -16.43) * mm});
            skLineSegment(sketch, "E1123", {"start": v(-28.04, -16.43) * mm, "end": v(-27.65, -16.57) * mm});
            skLineSegment(sketch, "E1124", {"start": v(-27.65, -16.57) * mm, "end": v(-27.52, -16.6) * mm});
            skLineSegment(sketch, "E1125", {"start": v(-27.52, -16.6) * mm, "end": v(-26.97, -16.83) * mm});
            skLineSegment(sketch, "E1126", {"start": v(-26.97, -16.83) * mm, "end": v(-26.8, -17.26) * mm});
            skLineSegment(sketch, "E1127", {"start": v(-26.8, -17.26) * mm, "end": v(-27.05, -17.75) * mm});
            skLineSegment(sketch, "E1128", {"start": v(-27.05, -17.75) * mm, "end": v(-27.73, -17.93) * mm});
            skLineSegment(sketch, "E1129", {"start": v(-27.73, -17.93) * mm, "end": v(-28.1, -17.9) * mm});
            skLineSegment(sketch, "E1130", {"start": v(-28.1, -17.9) * mm, "end": v(-28.51, -17.8) * mm});
            skLineSegment(sketch, "E1131", {"start": v(-28.51, -17.8) * mm, "end": v(-28.51, -17.41) * mm});
            skLineSegment(sketch, "E1132", {"start": v(-28.51, -17.41) * mm, "end": v(-28.11, -17.57) * mm});
            skLineSegment(sketch, "E1133", {"start": v(-28.11, -17.57) * mm, "end": v(-27.72, -17.62) * mm});
            skLineSegment(sketch, "E1134", {"start": v(-27.72, -17.62) * mm, "end": v(-27.32, -17.54) * mm});
            skLineSegment(sketch, "E1135", {"start": v(-27.32, -17.54) * mm, "end": v(-27.18, -17.29) * mm});
            skLineSegment(sketch, "E1136", {"start": v(-27.18, -17.29) * mm, "end": v(-27.28, -17.06) * mm});
            skLineSegment(sketch, "E1137", {"start": v(-27.28, -17.06) * mm, "end": v(-27.72, -16.9) * mm});
            skLineSegment(sketch, "E1138", {"start": v(-27.72, -16.9) * mm, "end": v(-27.85, -16.87) * mm});
            skLineSegment(sketch, "E1139", {"start": v(-27.85, -16.87) * mm, "end": v(-28.34, -16.65) * mm});
            skLineSegment(sketch, "E1140", {"start": v(-28.34, -16.65) * mm, "end": v(-28.5, -16.24) * mm});
            skLineSegment(sketch, "E1141", {"start": v(-28.5, -16.24) * mm, "end": v(-28.27, -15.76) * mm});
            skLineSegment(sketch, "E1142", {"start": v(-28.27, -15.76) * mm, "end": v(-27.64, -15.59) * mm});
            skLineSegment(sketch, "E1143", {"start": v(-27.64, -15.59) * mm, "end": v(-27.25, -15.62) * mm});
            skLineSegment(sketch, "E1144", {"start": v(-27.25, -15.62) * mm, "end": v(-26.92, -15.7) * mm});
            skLineSegment(sketch, "E1145", {"start": v(-24.36, -16.53) * mm, "end": v(-24.36, -17.87) * mm});
            skLineSegment(sketch, "E1146", {"start": v(-24.36, -17.87) * mm, "end": v(-24.73, -17.87) * mm});
            skLineSegment(sketch, "E1147", {"start": v(-24.73, -17.87) * mm, "end": v(-24.73, -16.54) * mm});
            skLineSegment(sketch, "E1148", {"start": v(-24.73, -16.54) * mm, "end": v(-24.85, -16.06) * mm});
            skLineSegment(sketch, "E1149", {"start": v(-24.85, -16.06) * mm, "end": v(-25.22, -15.9) * mm});
            skLineSegment(sketch, "E1150", {"start": v(-25.22, -15.9) * mm, "end": v(-25.7, -16.1) * mm});
            skLineSegment(sketch, "E1151", {"start": v(-25.7, -16.1) * mm, "end": v(-25.86, -16.61) * mm});
            skLineSegment(sketch, "E1152", {"start": v(-25.86, -16.61) * mm, "end": v(-25.86, -17.87) * mm});
            skLineSegment(sketch, "E1153", {"start": v(-25.86, -17.87) * mm, "end": v(-26.23, -17.87) * mm});
            skLineSegment(sketch, "E1154", {"start": v(-26.23, -17.87) * mm, "end": v(-26.23, -14.77) * mm});
            skLineSegment(sketch, "E1155", {"start": v(-26.23, -14.77) * mm, "end": v(-25.86, -14.77) * mm});
            skLineSegment(sketch, "E1156", {"start": v(-25.86, -14.77) * mm, "end": v(-25.86, -15.99) * mm});
            skLineSegment(sketch, "E1157", {"start": v(-25.86, -15.99) * mm, "end": v(-25.55, -15.69) * mm});
            skLineSegment(sketch, "E1158", {"start": v(-25.55, -15.69) * mm, "end": v(-25.14, -15.59) * mm});
            skLineSegment(sketch, "E1159", {"start": v(-25.14, -15.59) * mm, "end": v(-24.56, -15.83) * mm});
            skLineSegment(sketch, "E1160", {"start": v(-24.56, -15.83) * mm, "end": v(-24.36, -16.53) * mm});
            skLineSegment(sketch, "E1161", {"start": v(-7.25, -14.9) * mm, "end": v(-7.25, -15.3) * mm});
            skLineSegment(sketch, "E1162", {"start": v(-7.25, -15.3) * mm, "end": v(-7.68, -15.13) * mm});
            skLineSegment(sketch, "E1163", {"start": v(-7.68, -15.13) * mm, "end": v(-8.07, -15.08) * mm});
            skLineSegment(sketch, "E1164", {"start": v(-8.07, -15.08) * mm, "end": v(-8.58, -15.2) * mm});
            skLineSegment(sketch, "E1165", {"start": v(-8.58, -15.2) * mm, "end": v(-8.76, -15.57) * mm});
            skLineSegment(sketch, "E1166", {"start": v(-8.76, -15.57) * mm, "end": v(-8.64, -15.86) * mm});
            skLineSegment(sketch, "E1167", {"start": v(-8.64, -15.86) * mm, "end": v(-8.19, -16.03) * mm});
            skLineSegment(sketch, "E1168", {"start": v(-8.19, -16.03) * mm, "end": v(-7.95, -16.08) * mm});
            skLineSegment(sketch, "E1169", {"start": v(-7.95, -16.08) * mm, "end": v(-7.28, -16.38) * mm});
            skLineSegment(sketch, "E1170", {"start": v(-7.28, -16.38) * mm, "end": v(-7.07, -16.96) * mm});
            skLineSegment(sketch, "E1171", {"start": v(-7.07, -16.96) * mm, "end": v(-7.36, -17.61) * mm});
            skLineSegment(sketch, "E1172", {"start": v(-7.36, -17.61) * mm, "end": v(-8.2, -17.84) * mm});
            skLineSegment(sketch, "E1173", {"start": v(-8.2, -17.84) * mm, "end": v(-8.66, -17.79) * mm});
            skLineSegment(sketch, "E1174", {"start": v(-8.66, -17.79) * mm, "end": v(-9.15, -17.65) * mm});
            skLineSegment(sketch, "E1175", {"start": v(-9.15, -17.65) * mm, "end": v(-9.15, -17.23) * mm});
            skLineSegment(sketch, "E1176", {"start": v(-9.15, -17.23) * mm, "end": v(-8.67, -17.44) * mm});
            skLineSegment(sketch, "E1177", {"start": v(-8.67, -17.44) * mm, "end": v(-8.2, -17.5) * mm});
            skLineSegment(sketch, "E1178", {"start": v(-8.2, -17.5) * mm, "end": v(-7.68, -17.37) * mm});
            skLineSegment(sketch, "E1179", {"start": v(-7.68, -17.37) * mm, "end": v(-7.49, -16.99) * mm});
            skLineSegment(sketch, "E1180", {"start": v(-7.49, -16.99) * mm, "end": v(-7.62, -16.64) * mm});
            skLineSegment(sketch, "E1181", {"start": v(-7.62, -16.64) * mm, "end": v(-8.06, -16.46) * mm});
            skLineSegment(sketch, "E1182", {"start": v(-8.06, -16.46) * mm, "end": v(-8.3, -16.41) * mm});
            skLineSegment(sketch, "E1183", {"start": v(-8.3, -16.41) * mm, "end": v(-8.96, -16.13) * mm});
            skLineSegment(sketch, "E1184", {"start": v(-8.96, -16.13) * mm, "end": v(-9.16, -15.6) * mm});
            skLineSegment(sketch, "E1185", {"start": v(-9.16, -15.6) * mm, "end": v(-8.88, -14.98) * mm});
            skLineSegment(sketch, "E1186", {"start": v(-8.88, -14.98) * mm, "end": v(-8.12, -14.75) * mm});
            skLineSegment(sketch, "E1187", {"start": v(-8.12, -14.75) * mm, "end": v(-7.7, -14.79) * mm});
            skLineSegment(sketch, "E1188", {"start": v(-7.7, -14.79) * mm, "end": v(-7.25, -14.9) * mm});
            skLineSegment(sketch, "E1189", {"start": v(-5.53, -17.99) * mm, "end": v(-5.83, -18.5) * mm});
            skLineSegment(sketch, "E1190", {"start": v(-5.83, -18.5) * mm, "end": v(-6.22, -18.63) * mm});
            skLineSegment(sketch, "E1191", {"start": v(-6.22, -18.63) * mm, "end": v(-6.52, -18.63) * mm});
            skLineSegment(sketch, "E1192", {"start": v(-6.52, -18.63) * mm, "end": v(-6.52, -18.32) * mm});
            skLineSegment(sketch, "E1193", {"start": v(-6.52, -18.32) * mm, "end": v(-6.3, -18.32) * mm});
            skLineSegment(sketch, "E1194", {"start": v(-6.3, -18.32) * mm, "end": v(-6.07, -18.25) * mm});
            skLineSegment(sketch, "E1195", {"start": v(-6.07, -18.25) * mm, "end": v(-5.88, -17.91) * mm});
            skLineSegment(sketch, "E1196", {"start": v(-5.88, -17.91) * mm, "end": v(-5.81, -17.74) * mm});
            skLineSegment(sketch, "E1197", {"start": v(-5.81, -17.74) * mm, "end": v(-6.72, -15.55) * mm});
            skLineSegment(sketch, "E1198", {"start": v(-6.72, -15.55) * mm, "end": v(-6.33, -15.55) * mm});
            skLineSegment(sketch, "E1199", {"start": v(-6.33, -15.55) * mm, "end": v(-5.63, -17.3) * mm});
            skLineSegment(sketch, "E1200", {"start": v(-5.63, -17.3) * mm, "end": v(-4.93, -15.55) * mm});
            skLineSegment(sketch, "E1201", {"start": v(-4.93, -15.55) * mm, "end": v(-4.54, -15.55) * mm});
            skLineSegment(sketch, "E1202", {"start": v(-4.54, -15.55) * mm, "end": v(-5.53, -17.99) * mm});
            skLineSegment(sketch, "E1203", {"start": v(-2.18, -16.43) * mm, "end": v(-2.18, -17.78) * mm});
            skLineSegment(sketch, "E1204", {"start": v(-2.18, -17.78) * mm, "end": v(-2.55, -17.78) * mm});
            skLineSegment(sketch, "E1205", {"start": v(-2.55, -17.78) * mm, "end": v(-2.55, -16.44) * mm});
            skLineSegment(sketch, "E1206", {"start": v(-2.55, -16.44) * mm, "end": v(-2.67, -15.97) * mm});
            skLineSegment(sketch, "E1207", {"start": v(-2.67, -15.97) * mm, "end": v(-3.04, -15.81) * mm});
            skLineSegment(sketch, "E1208", {"start": v(-3.04, -15.81) * mm, "end": v(-3.51, -16) * mm});
            skLineSegment(sketch, "E1209", {"start": v(-3.51, -16) * mm, "end": v(-3.68, -16.52) * mm});
            skLineSegment(sketch, "E1210", {"start": v(-3.68, -16.52) * mm, "end": v(-3.68, -17.78) * mm});
            skLineSegment(sketch, "E1211", {"start": v(-3.68, -17.78) * mm, "end": v(-4.05, -17.78) * mm});
            skLineSegment(sketch, "E1212", {"start": v(-4.05, -17.78) * mm, "end": v(-4.05, -15.55) * mm});
            skLineSegment(sketch, "E1213", {"start": v(-4.05, -15.55) * mm, "end": v(-3.68, -15.55) * mm});
            skLineSegment(sketch, "E1214", {"start": v(-3.68, -15.55) * mm, "end": v(-3.68, -15.9) * mm});
            skLineSegment(sketch, "E1215", {"start": v(-3.68, -15.9) * mm, "end": v(-3.37, -15.6) * mm});
            skLineSegment(sketch, "E1216", {"start": v(-3.37, -15.6) * mm, "end": v(-2.96, -15.5) * mm});
            skLineSegment(sketch, "E1217", {"start": v(-2.96, -15.5) * mm, "end": v(-2.38, -15.73) * mm});
            skLineSegment(sketch, "E1218", {"start": v(-2.38, -15.73) * mm, "end": v(-2.18, -16.43) * mm});
            skLineSegment(sketch, "E1219", {"start": v(0.16, -15.63) * mm, "end": v(0.16, -15.97) * mm});
            skLineSegment(sketch, "E1220", {"start": v(0.16, -15.97) * mm, "end": v(-0.15, -15.85) * mm});
            skLineSegment(sketch, "E1221", {"start": v(-0.15, -15.85) * mm, "end": v(-0.47, -15.8) * mm});
            skLineSegment(sketch, "E1222", {"start": v(-0.47, -15.8) * mm, "end": v(-1.02, -16.03) * mm});
            skLineSegment(sketch, "E1223", {"start": v(-1.02, -16.03) * mm, "end": v(-1.22, -16.66) * mm});
            skLineSegment(sketch, "E1224", {"start": v(-1.22, -16.66) * mm, "end": v(-1.02, -17.3) * mm});
            skLineSegment(sketch, "E1225", {"start": v(-1.02, -17.3) * mm, "end": v(-0.47, -17.53) * mm});
            skLineSegment(sketch, "E1226", {"start": v(-0.47, -17.53) * mm, "end": v(-0.15, -17.48) * mm});
            skLineSegment(sketch, "E1227", {"start": v(-0.15, -17.48) * mm, "end": v(0.16, -17.35) * mm});
            skLineSegment(sketch, "E1228", {"start": v(0.16, -17.35) * mm, "end": v(0.16, -17.7) * mm});
            skLineSegment(sketch, "E1229", {"start": v(0.16, -17.7) * mm, "end": v(-0.16, -17.8) * mm});
            skLineSegment(sketch, "E1230", {"start": v(-0.16, -17.8) * mm, "end": v(-0.5, -17.84) * mm});
            skLineSegment(sketch, "E1231", {"start": v(-0.5, -17.84) * mm, "end": v(-1.3, -17.52) * mm});
            skLineSegment(sketch, "E1232", {"start": v(-1.3, -17.52) * mm, "end": v(-1.6, -16.66) * mm});
            skLineSegment(sketch, "E1233", {"start": v(-1.6, -16.66) * mm, "end": v(-1.3, -15.8) * mm});
            skLineSegment(sketch, "E1234", {"start": v(-1.3, -15.8) * mm, "end": v(-0.48, -15.5) * mm});
            skLineSegment(sketch, "E1235", {"start": v(-0.48, -15.5) * mm, "end": v(-0.15, -15.53) * mm});
            skLineSegment(sketch, "E1236", {"start": v(-0.15, -15.53) * mm, "end": v(0.16, -15.63) * mm});
            skSolve(sketch);
        }
        {
            var Q0;
            Q0 = qSketchRegion(id + "F2", true);
            extrude(context, id + "F3", {"entities" : qUnion([Q0]), "depth" : 0.1 * mm, "offsetDistance" : 25 * mm});
        }
    });
